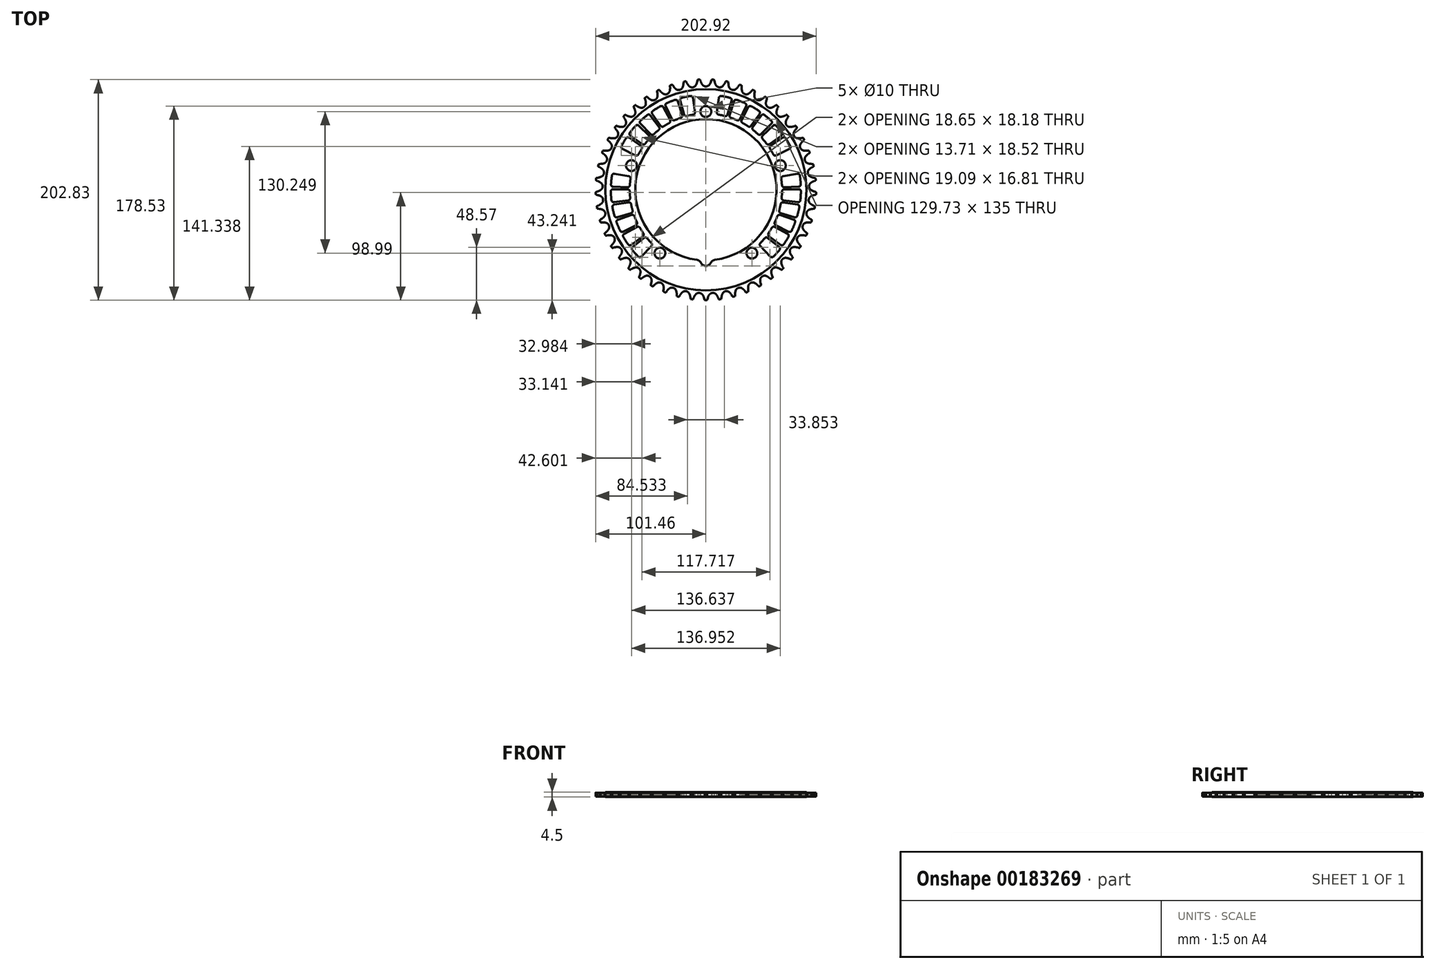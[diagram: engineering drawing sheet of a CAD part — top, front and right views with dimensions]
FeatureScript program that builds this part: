
annotation { "Feature Type Name" : "Feature", "Feature Type Description" : "" }
export const myFeature = defineFeature(function(context is Context, id is Id, definition is map)
    precondition{}
    {
        {
            var Q0;
            Q0=qCreatedBy(makeId("Top.planeOp"),FACE);
            var sketch = newSketch(context, id + "F0", { "sketchPlane" : qUnion([Q0])});
            skCircle(sketch, "E0", {"center": v(0, 0) * mm, "radius": 65 * mm});
            skCircle(sketch, "E1", {"center": v(0, 72) * mm, "radius": 5 * mm});
            skCircle(sketch, "E2.1.0", {"center": v(-68.48, 22.25) * mm, "radius": 5 * mm});
            skCircle(sketch, "E2.2.0", {"center": v(-42.32, -58.25) * mm, "radius": 5 * mm});
            skCircle(sketch, "E2.3.0", {"center": v(42.32, -58.25) * mm, "radius": 5 * mm});
            skCircle(sketch, "E2.4.0", {"center": v(68.48, 22.25) * mm, "radius": 5 * mm});
            skArc(sketch, "E3", {"start": v(-3.24, 96.67) * mm, "mid": v(-1.82, 95.46) * mm, "end": v(0, 95.03) * mm});
            skCircle(sketch, "E4", {"center": v(0, 0) * mm, "radius": 92.53 * mm});
            skCircle(sketch, "E5", {"center": v(0, -65) * mm, "radius": 5 * mm});
            skArc(sketch, "E6", {"start": v(-4.67, 99.35) * mm, "mid": v(-4.06, 97.96) * mm, "end": v(-3.24, 96.67) * mm});
            skLineSegment(sketch, "E7", {"start": v(-4.67, 99.35) * mm, "end": v(-5.06, 100.45) * mm});
            skArc(sketch, "E8", {"start": v(-5.06, 100.45) * mm, "mid": v(-5.7, 101.76) * mm, "end": v(-6.6, 102.9) * mm});
            skArc(sketch, "E9.MirrorCS", {"start": v(5.06, 100.45) * mm, "mid": v(5.7, 101.76) * mm, "end": v(6.6, 102.9) * mm});
            skLineSegment(sketch, "E10.MirrorCS", {"start": v(4.67, 99.35) * mm, "end": v(5.06, 100.45) * mm});
            skArc(sketch, "E11.MirrorCS", {"start": v(4.67, 99.35) * mm, "mid": v(4.06, 97.96) * mm, "end": v(3.24, 96.67) * mm});
            skArc(sketch, "E12.MirrorCS", {"start": v(3.24, 96.67) * mm, "mid": v(1.82, 95.46) * mm, "end": v(0, 95.03) * mm});
            skArc(sketch, "E13.1.0", {"start": v(-17.87, 98.98) * mm, "mid": v(-18.66, 100.2) * mm, "end": v(-19.7, 101.2) * mm});
            skLineSegment(sketch, "E13.1.1", {"start": v(-17.34, 97.94) * mm, "end": v(-17.87, 98.98) * mm});
            skArc(sketch, "E13.1.2", {"start": v(-17.34, 97.94) * mm, "mid": v(-16.55, 96.64) * mm, "end": v(-15.57, 95.46) * mm});
            skArc(sketch, "E13.1.3", {"start": v(-15.57, 95.46) * mm, "mid": v(-14, 94.45) * mm, "end": v(-12.15, 94.25) * mm});
            skArc(sketch, "E13.1.4", {"start": v(-9.15, 96.29) * mm, "mid": v(-10.4, 94.9) * mm, "end": v(-12.15, 94.25) * mm});
            skArc(sketch, "E13.1.5", {"start": v(-8.07, 99.14) * mm, "mid": v(-8.5, 97.67) * mm, "end": v(-9.15, 96.29) * mm});
            skLineSegment(sketch, "E13.1.6", {"start": v(-8.07, 99.14) * mm, "end": v(-7.83, 100.28) * mm});
            skArc(sketch, "E13.1.7", {"start": v(-7.83, 100.28) * mm, "mid": v(-7.37, 101.65) * mm, "end": v(-6.6, 102.9) * mm});
            skArc(sketch, "E13.2.0", {"start": v(-30.38, 95.89) * mm, "mid": v(-31.32, 96.99) * mm, "end": v(-32.49, 97.85) * mm});
            skLineSegment(sketch, "E13.2.1", {"start": v(-29.72, 94.92) * mm, "end": v(-30.38, 95.89) * mm});
            skArc(sketch, "E13.2.2", {"start": v(-29.72, 94.92) * mm, "mid": v(-28.77, 93.73) * mm, "end": v(-27.65, 92.69) * mm});
            skArc(sketch, "E13.2.3", {"start": v(-27.65, 92.69) * mm, "mid": v(-25.97, 91.88) * mm, "end": v(-24.1, 91.92) * mm});
            skArc(sketch, "E13.2.4", {"start": v(-21.39, 94.33) * mm, "mid": v(-22.46, 92.8) * mm, "end": v(-24.1, 91.92) * mm});
            skArc(sketch, "E13.2.5", {"start": v(-20.68, 97.3) * mm, "mid": v(-20.92, 95.78) * mm, "end": v(-21.39, 94.33) * mm});
            skLineSegment(sketch, "E13.2.6", {"start": v(-20.68, 97.3) * mm, "end": v(-20.59, 98.45) * mm});
            skArc(sketch, "E13.2.7", {"start": v(-20.59, 98.45) * mm, "mid": v(-20.3, 99.88) * mm, "end": v(-19.7, 101.2) * mm});
            skArc(sketch, "E13.3.0", {"start": v(-42.39, 91.21) * mm, "mid": v(-43.47, 92.19) * mm, "end": v(-44.73, 92.9) * mm});
            skLineSegment(sketch, "E13.3.1", {"start": v(-41.62, 90.34) * mm, "end": v(-42.39, 91.21) * mm});
            skArc(sketch, "E13.3.2", {"start": v(-41.62, 90.34) * mm, "mid": v(-40.52, 89.28) * mm, "end": v(-39.28, 88.39) * mm});
            skArc(sketch, "E13.3.3", {"start": v(-39.28, 88.39) * mm, "mid": v(-37.5, 87.8) * mm, "end": v(-35.66, 88.08) * mm});
            skArc(sketch, "E13.3.4", {"start": v(-33.27, 90.82) * mm, "mid": v(-34.14, 89.17) * mm, "end": v(-35.66, 88.08) * mm});
            skArc(sketch, "E13.3.5", {"start": v(-32.95, 93.85) * mm, "mid": v(-33, 92.32) * mm, "end": v(-33.27, 90.82) * mm});
            skLineSegment(sketch, "E13.3.6", {"start": v(-32.95, 93.85) * mm, "end": v(-33, 95.01) * mm});
            skArc(sketch, "E13.3.7", {"start": v(-33, 95.01) * mm, "mid": v(-32.9, 96.46) * mm, "end": v(-32.49, 97.85) * mm});
            skArc(sketch, "E13.4.0", {"start": v(-53.7, 85.04) * mm, "mid": v(-54.9, 85.87) * mm, "end": v(-56.25, 86.4) * mm});
            skLineSegment(sketch, "E13.4.1", {"start": v(-52.83, 84.28) * mm, "end": v(-53.7, 85.04) * mm});
            skArc(sketch, "E13.4.2", {"start": v(-52.83, 84.28) * mm, "mid": v(-51.6, 83.36) * mm, "end": v(-50.26, 82.64) * mm});
            skArc(sketch, "E13.4.3", {"start": v(-50.26, 82.64) * mm, "mid": v(-48.43, 82.29) * mm, "end": v(-46.63, 82.8) * mm});
            skArc(sketch, "E13.4.4", {"start": v(-44.62, 85.82) * mm, "mid": v(-45.26, 84.07) * mm, "end": v(-46.63, 82.8) * mm});
            skArc(sketch, "E13.4.5", {"start": v(-44.68, 88.86) * mm, "mid": v(-44.54, 87.34) * mm, "end": v(-44.62, 85.82) * mm});
            skLineSegment(sketch, "E13.4.6", {"start": v(-44.68, 88.86) * mm, "end": v(-44.88, 90.01) * mm});
            skArc(sketch, "E13.4.7", {"start": v(-44.88, 90.01) * mm, "mid": v(-44.97, 91.46) * mm, "end": v(-44.73, 92.9) * mm});
            skArc(sketch, "E13.5.0", {"start": v(-64.14, 77.48) * mm, "mid": v(-65.43, 78.15) * mm, "end": v(-66.83, 78.5) * mm});
            skLineSegment(sketch, "E13.5.1", {"start": v(-63.17, 76.83) * mm, "end": v(-64.14, 77.48) * mm});
            skArc(sketch, "E13.5.2", {"start": v(-63.17, 76.83) * mm, "mid": v(-61.84, 76.08) * mm, "end": v(-60.41, 75.53) * mm});
            skArc(sketch, "E13.5.3", {"start": v(-60.41, 75.53) * mm, "mid": v(-58.55, 75.42) * mm, "end": v(-56.84, 76.16) * mm});
            skArc(sketch, "E13.5.4", {"start": v(-55.22, 79.4) * mm, "mid": v(-55.64, 77.59) * mm, "end": v(-56.84, 76.16) * mm});
            skArc(sketch, "E13.5.5", {"start": v(-55.68, 82.42) * mm, "mid": v(-55.34, 80.93) * mm, "end": v(-55.22, 79.4) * mm});
            skLineSegment(sketch, "E13.5.6", {"start": v(-55.68, 82.42) * mm, "end": v(-56.03, 83.53) * mm});
            skArc(sketch, "E13.5.7", {"start": v(-56.03, 83.53) * mm, "mid": v(-56.3, 84.96) * mm, "end": v(-56.25, 86.4) * mm});
            skArc(sketch, "E13.6.0", {"start": v(-73.52, 68.64) * mm, "mid": v(-74.88, 69.14) * mm, "end": v(-76.32, 69.32) * mm});
            skLineSegment(sketch, "E13.6.1", {"start": v(-72.48, 68.12) * mm, "end": v(-73.52, 68.64) * mm});
            skArc(sketch, "E13.6.2", {"start": v(-72.48, 68.12) * mm, "mid": v(-71.06, 67.55) * mm, "end": v(-69.58, 67.19) * mm});
            skArc(sketch, "E13.6.3", {"start": v(-69.58, 67.19) * mm, "mid": v(-67.71, 67.31) * mm, "end": v(-66.1, 68.26) * mm});
            skArc(sketch, "E13.6.4", {"start": v(-64.92, 71.7) * mm, "mid": v(-65.1, 69.84) * mm, "end": v(-66.1, 68.26) * mm});
            skArc(sketch, "E13.6.5", {"start": v(-65.76, 74.62) * mm, "mid": v(-65.23, 73.2) * mm, "end": v(-64.92, 71.7) * mm});
            skLineSegment(sketch, "E13.6.6", {"start": v(-65.76, 74.62) * mm, "end": v(-66.25, 75.68) * mm});
            skArc(sketch, "E13.6.7", {"start": v(-66.25, 75.68) * mm, "mid": v(-66.7, 77.06) * mm, "end": v(-66.83, 78.5) * mm});
            skArc(sketch, "E13.7.0", {"start": v(-81.7, 58.68) * mm, "mid": v(-83.11, 59) * mm, "end": v(-84.56, 58.99) * mm});
            skLineSegment(sketch, "E13.7.1", {"start": v(-80.6, 58.3) * mm, "end": v(-81.7, 58.68) * mm});
            skArc(sketch, "E13.7.2", {"start": v(-80.6, 58.3) * mm, "mid": v(-79.12, 57.9) * mm, "end": v(-77.6, 57.74) * mm});
            skArc(sketch, "E13.7.3", {"start": v(-77.6, 57.74) * mm, "mid": v(-75.77, 58.1) * mm, "end": v(-74.3, 59.25) * mm});
            skArc(sketch, "E13.7.4", {"start": v(-73.56, 62.8) * mm, "mid": v(-73.5, 60.94) * mm, "end": v(-74.3, 59.25) * mm});
            skArc(sketch, "E13.7.5", {"start": v(-74.76, 65.6) * mm, "mid": v(-74.06, 64.25) * mm, "end": v(-73.56, 62.8) * mm});
            skLineSegment(sketch, "E13.7.6", {"start": v(-74.76, 65.6) * mm, "end": v(-75.38, 66.59) * mm});
            skArc(sketch, "E13.7.7", {"start": v(-75.38, 66.59) * mm, "mid": v(-76, 67.9) * mm, "end": v(-76.32, 69.32) * mm});
            skArc(sketch, "E13.8.0", {"start": v(-88.53, 47.75) * mm, "mid": v(-89.97, 47.88) * mm, "end": v(-91.41, 47.69) * mm});
            skLineSegment(sketch, "E13.8.1", {"start": v(-87.38, 47.5) * mm, "end": v(-88.53, 47.75) * mm});
            skArc(sketch, "E13.8.2", {"start": v(-87.38, 47.5) * mm, "mid": v(-85.87, 47.31) * mm, "end": v(-84.35, 47.34) * mm});
            skArc(sketch, "E13.8.3", {"start": v(-84.35, 47.34) * mm, "mid": v(-82.57, 47.93) * mm, "end": v(-81.26, 49.26) * mm});
            skArc(sketch, "E13.8.4", {"start": v(-80.99, 52.88) * mm, "mid": v(-80.7, 51.04) * mm, "end": v(-81.26, 49.26) * mm});
            skArc(sketch, "E13.8.5", {"start": v(-82.54, 55.5) * mm, "mid": v(-81.67, 54.25) * mm, "end": v(-80.99, 52.88) * mm});
            skLineSegment(sketch, "E13.8.6", {"start": v(-82.54, 55.5) * mm, "end": v(-83.28, 56.4) * mm});
            skArc(sketch, "E13.8.7", {"start": v(-83.28, 56.4) * mm, "mid": v(-84.07, 57.62) * mm, "end": v(-84.56, 58.99) * mm});
            skArc(sketch, "E13.9.0", {"start": v(-93.9, 36.03) * mm, "mid": v(-95.36, 35.98) * mm, "end": v(-96.76, 35.6) * mm});
            skLineSegment(sketch, "E13.9.1", {"start": v(-92.74, 35.94) * mm, "end": v(-93.9, 36.03) * mm});
            skArc(sketch, "E13.9.2", {"start": v(-92.74, 35.94) * mm, "mid": v(-91.22, 35.94) * mm, "end": v(-89.7, 36.17) * mm});
            skArc(sketch, "E13.9.3", {"start": v(-89.7, 36.17) * mm, "mid": v(-88.03, 36.98) * mm, "end": v(-86.9, 38.47) * mm});
            skArc(sketch, "E13.9.4", {"start": v(-87.08, 42.1) * mm, "mid": v(-86.56, 40.3) * mm, "end": v(-86.9, 38.47) * mm});
            skArc(sketch, "E13.9.5", {"start": v(-88.96, 44.5) * mm, "mid": v(-87.93, 43.36) * mm, "end": v(-87.08, 42.1) * mm});
            skLineSegment(sketch, "E13.9.6", {"start": v(-88.96, 44.5) * mm, "end": v(-89.8, 45.3) * mm});
            skArc(sketch, "E13.9.7", {"start": v(-89.8, 45.3) * mm, "mid": v(-90.75, 46.4) * mm, "end": v(-91.41, 47.69) * mm});
            skArc(sketch, "E13.10.0", {"start": v(-97.74, 23.73) * mm, "mid": v(-99.17, 23.5) * mm, "end": v(-100.52, 22.94) * mm});
            skLineSegment(sketch, "E13.10.1", {"start": v(-96.58, 23.79) * mm, "end": v(-97.74, 23.73) * mm});
            skArc(sketch, "E13.10.2", {"start": v(-96.58, 23.79) * mm, "mid": v(-95.06, 23.98) * mm, "end": v(-93.6, 24.4) * mm});
            skArc(sketch, "E13.10.3", {"start": v(-93.6, 24.4) * mm, "mid": v(-92.03, 25.42) * mm, "end": v(-91.1, 27.04) * mm});
            skArc(sketch, "E13.10.4", {"start": v(-91.75, 30.61) * mm, "mid": v(-91, 28.9) * mm, "end": v(-91.1, 27.04) * mm});
            skArc(sketch, "E13.10.5", {"start": v(-93.92, 32.75) * mm, "mid": v(-92.76, 31.76) * mm, "end": v(-91.75, 30.61) * mm});
            skLineSegment(sketch, "E13.10.6", {"start": v(-93.92, 32.75) * mm, "end": v(-94.86, 33.43) * mm});
            skArc(sketch, "E13.10.7", {"start": v(-94.86, 33.43) * mm, "mid": v(-95.93, 34.41) * mm, "end": v(-96.76, 35.6) * mm});
            skArc(sketch, "E13.11.0", {"start": v(-99.97, 11.04) * mm, "mid": v(-101.37, 10.62) * mm, "end": v(-102.63, 9.9) * mm});
            skLineSegment(sketch, "E13.11.1", {"start": v(-98.83, 11.24) * mm, "end": v(-99.97, 11.04) * mm});
            skArc(sketch, "E13.11.2", {"start": v(-98.83, 11.24) * mm, "mid": v(-97.35, 11.63) * mm, "end": v(-95.95, 12.23) * mm});
            skArc(sketch, "E13.11.3", {"start": v(-95.95, 12.23) * mm, "mid": v(-94.53, 13.44) * mm, "end": v(-93.8, 15.17) * mm});
            skArc(sketch, "E13.11.4", {"start": v(-94.91, 18.63) * mm, "mid": v(-93.95, 17.03) * mm, "end": v(-93.8, 15.17) * mm});
            skArc(sketch, "E13.11.5", {"start": v(-97.33, 20.47) * mm, "mid": v(-96.06, 19.64) * mm, "end": v(-94.91, 18.63) * mm});
            skLineSegment(sketch, "E13.11.6", {"start": v(-97.33, 20.47) * mm, "end": v(-98.36, 21.03) * mm});
            skArc(sketch, "E13.11.7", {"start": v(-98.36, 21.03) * mm, "mid": v(-99.55, 21.86) * mm, "end": v(-100.52, 22.94) * mm});
            skArc(sketch, "E13.12.0", {"start": v(-100.56, -1.84) * mm, "mid": v(-101.9, -2.43) * mm, "end": v(-103.05, -3.3) * mm});
            skLineSegment(sketch, "E13.12.1", {"start": v(-99.45, -1.49) * mm, "end": v(-100.56, -1.84) * mm});
            skArc(sketch, "E13.12.2", {"start": v(-99.45, -1.49) * mm, "mid": v(-98.04, -0.91) * mm, "end": v(-96.72, -0.14) * mm});
            skArc(sketch, "E13.12.3", {"start": v(-96.72, -0.14) * mm, "mid": v(-95.47, 1.24) * mm, "end": v(-94.98, 3.05) * mm});
            skArc(sketch, "E13.12.4", {"start": v(-96.52, 6.34) * mm, "mid": v(-95.35, 4.87) * mm, "end": v(-94.98, 3.05) * mm});
            skArc(sketch, "E13.12.5", {"start": v(-99.15, 7.86) * mm, "mid": v(-97.78, 7.2) * mm, "end": v(-96.52, 6.34) * mm});
            skLineSegment(sketch, "E13.12.6", {"start": v(-99.15, 7.86) * mm, "end": v(-100.24, 8.28) * mm});
            skArc(sketch, "E13.12.7", {"start": v(-100.24, 8.28) * mm, "mid": v(-101.53, 8.95) * mm, "end": v(-102.63, 9.9) * mm});
            skArc(sketch, "E13.13.0", {"start": v(-99.5, -14.68) * mm, "mid": v(-100.74, -15.44) * mm, "end": v(-101.78, -16.46) * mm});
            skLineSegment(sketch, "E13.13.1", {"start": v(-98.45, -14.2) * mm, "end": v(-99.5, -14.68) * mm});
            skArc(sketch, "E13.13.2", {"start": v(-98.45, -14.2) * mm, "mid": v(-97.12, -13.44) * mm, "end": v(-95.91, -12.5) * mm});
            skArc(sketch, "E13.13.3", {"start": v(-95.91, -12.5) * mm, "mid": v(-94.85, -10.97) * mm, "end": v(-94.59, -9.12) * mm});
            skArc(sketch, "E13.13.4", {"start": v(-96.53, -6.06) * mm, "mid": v(-95.2, -7.36) * mm, "end": v(-94.59, -9.12) * mm});
            skArc(sketch, "E13.13.5", {"start": v(-99.34, -4.89) * mm, "mid": v(-97.9, -5.37) * mm, "end": v(-96.53, -6.06) * mm});
            skLineSegment(sketch, "E13.13.6", {"start": v(-99.34, -4.89) * mm, "end": v(-100.48, -4.6) * mm});
            skArc(sketch, "E13.13.7", {"start": v(-100.48, -4.6) * mm, "mid": v(-101.84, -4.1) * mm, "end": v(-103.05, -3.3) * mm});
            skArc(sketch, "E13.14.0", {"start": v(-96.8, -27.29) * mm, "mid": v(-97.94, -28.2) * mm, "end": v(-98.84, -29.34) * mm});
            skLineSegment(sketch, "E13.14.1", {"start": v(-95.82, -26.67) * mm, "end": v(-96.8, -27.29) * mm});
            skArc(sketch, "E13.14.2", {"start": v(-95.82, -26.67) * mm, "mid": v(-94.6, -25.75) * mm, "end": v(-93.52, -24.67) * mm});
            skArc(sketch, "E13.14.3", {"start": v(-93.52, -24.67) * mm, "mid": v(-92.66, -23.01) * mm, "end": v(-92.64, -21.15) * mm});
            skArc(sketch, "E13.14.4", {"start": v(-94.97, -18.35) * mm, "mid": v(-93.47, -19.47) * mm, "end": v(-92.64, -21.15) * mm});
            skArc(sketch, "E13.14.5", {"start": v(-97.9, -17.55) * mm, "mid": v(-96.4, -17.84) * mm, "end": v(-94.97, -18.35) * mm});
            skLineSegment(sketch, "E13.14.6", {"start": v(-97.9, -17.55) * mm, "end": v(-99.06, -17.42) * mm});
            skArc(sketch, "E13.14.7", {"start": v(-99.06, -17.42) * mm, "mid": v(-100.48, -17.1) * mm, "end": v(-101.78, -16.46) * mm});
            skArc(sketch, "E13.15.0", {"start": v(-92.53, -39.44) * mm, "mid": v(-93.53, -40.49) * mm, "end": v(-94.28, -41.73) * mm});
            skLineSegment(sketch, "E13.15.1", {"start": v(-91.63, -38.7) * mm, "end": v(-92.53, -39.44) * mm});
            skArc(sketch, "E13.15.2", {"start": v(-91.63, -38.7) * mm, "mid": v(-90.53, -37.64) * mm, "end": v(-89.6, -36.43) * mm});
            skArc(sketch, "E13.15.3", {"start": v(-89.6, -36.43) * mm, "mid": v(-88.96, -34.67) * mm, "end": v(-89.18, -32.82) * mm});
            skArc(sketch, "E13.15.4", {"start": v(-91.84, -30.35) * mm, "mid": v(-90.21, -31.26) * mm, "end": v(-89.18, -32.82) * mm});
            skArc(sketch, "E13.15.5", {"start": v(-94.85, -29.93) * mm, "mid": v(-93.33, -30.03) * mm, "end": v(-91.84, -30.35) * mm});
            skLineSegment(sketch, "E13.15.6", {"start": v(-94.85, -29.93) * mm, "end": v(-96.02, -29.94) * mm});
            skArc(sketch, "E13.15.7", {"start": v(-96.02, -29.94) * mm, "mid": v(-97.47, -29.8) * mm, "end": v(-98.84, -29.34) * mm});
            skArc(sketch, "E13.16.0", {"start": v(-86.72, -50.95) * mm, "mid": v(-87.59, -52.12) * mm, "end": v(-88.17, -53.45) * mm});
            skLineSegment(sketch, "E13.16.1", {"start": v(-85.93, -50.1) * mm, "end": v(-86.72, -50.95) * mm});
            skArc(sketch, "E13.16.2", {"start": v(-85.93, -50.1) * mm, "mid": v(-84.97, -48.9) * mm, "end": v(-84.2, -47.59) * mm});
            skArc(sketch, "E13.16.3", {"start": v(-84.2, -47.59) * mm, "mid": v(-83.8, -45.76) * mm, "end": v(-84.25, -43.95) * mm});
            skArc(sketch, "E13.16.4", {"start": v(-87.2, -41.84) * mm, "mid": v(-85.48, -42.54) * mm, "end": v(-84.25, -43.95) * mm});
            skArc(sketch, "E13.16.5", {"start": v(-90.25, -41.81) * mm, "mid": v(-88.73, -41.71) * mm, "end": v(-87.2, -41.84) * mm});
            skLineSegment(sketch, "E13.16.6", {"start": v(-90.25, -41.81) * mm, "end": v(-91.4, -41.98) * mm});
            skArc(sketch, "E13.16.7", {"start": v(-91.4, -41.98) * mm, "mid": v(-92.85, -42.02) * mm, "end": v(-94.28, -41.73) * mm});
            skArc(sketch, "E13.17.0", {"start": v(-79.5, -61.62) * mm, "mid": v(-80.2, -62.89) * mm, "end": v(-80.6, -64.28) * mm});
            skLineSegment(sketch, "E13.17.1", {"start": v(-78.81, -60.68) * mm, "end": v(-79.5, -61.62) * mm});
            skArc(sketch, "E13.17.2", {"start": v(-78.81, -60.68) * mm, "mid": v(-78.02, -59.37) * mm, "end": v(-77.43, -57.96) * mm});
            skArc(sketch, "E13.17.3", {"start": v(-77.43, -57.96) * mm, "mid": v(-77.26, -56.1) * mm, "end": v(-77.94, -54.37) * mm});
            skArc(sketch, "E13.17.4", {"start": v(-81.14, -52.65) * mm, "mid": v(-79.33, -53.13) * mm, "end": v(-77.94, -54.37) * mm});
            skArc(sketch, "E13.17.5", {"start": v(-84.16, -53) * mm, "mid": v(-82.66, -52.72) * mm, "end": v(-81.14, -52.65) * mm});
            skLineSegment(sketch, "E13.17.6", {"start": v(-84.16, -53) * mm, "end": v(-85.29, -53.32) * mm});
            skArc(sketch, "E13.17.7", {"start": v(-85.29, -53.32) * mm, "mid": v(-86.72, -53.55) * mm, "end": v(-88.17, -53.45) * mm});
            skArc(sketch, "E13.18.0", {"start": v(-70.96, -71.28) * mm, "mid": v(-71.5, -72.63) * mm, "end": v(-71.73, -74.06) * mm});
            skLineSegment(sketch, "E13.18.1", {"start": v(-70.4, -70.26) * mm, "end": v(-70.96, -71.28) * mm});
            skArc(sketch, "E13.18.2", {"start": v(-70.4, -70.26) * mm, "mid": v(-69.8, -68.86) * mm, "end": v(-69.38, -67.39) * mm});
            skArc(sketch, "E13.18.3", {"start": v(-69.38, -67.39) * mm, "mid": v(-69.45, -65.52) * mm, "end": v(-70.35, -63.89) * mm});
            skArc(sketch, "E13.18.4", {"start": v(-73.74, -62.6) * mm, "mid": v(-71.89, -62.83) * mm, "end": v(-70.35, -63.89) * mm});
            skArc(sketch, "E13.18.5", {"start": v(-76.7, -63.34) * mm, "mid": v(-75.24, -62.86) * mm, "end": v(-73.74, -62.6) * mm});
            skLineSegment(sketch, "E13.18.6", {"start": v(-76.7, -63.34) * mm, "end": v(-77.77, -63.79) * mm});
            skArc(sketch, "E13.18.7", {"start": v(-77.77, -63.79) * mm, "mid": v(-79.16, -64.2) * mm, "end": v(-80.6, -64.28) * mm});
            skArc(sketch, "E13.19.0", {"start": v(-61.26, -79.77) * mm, "mid": v(-61.63, -81.18) * mm, "end": v(-61.67, -82.63) * mm});
            skLineSegment(sketch, "E13.19.1", {"start": v(-60.84, -78.68) * mm, "end": v(-61.26, -79.77) * mm});
            skArc(sketch, "E13.19.2", {"start": v(-60.84, -78.68) * mm, "mid": v(-60.41, -77.22) * mm, "end": v(-60.2, -75.7) * mm});
            skArc(sketch, "E13.19.3", {"start": v(-60.2, -75.7) * mm, "mid": v(-60.5, -73.87) * mm, "end": v(-61.6, -72.36) * mm});
            skArc(sketch, "E13.19.4", {"start": v(-65.13, -71.5) * mm, "mid": v(-63.26, -71.51) * mm, "end": v(-61.6, -72.36) * mm});
            skArc(sketch, "E13.19.5", {"start": v(-67.96, -72.62) * mm, "mid": v(-66.59, -71.96) * mm, "end": v(-65.13, -71.5) * mm});
            skLineSegment(sketch, "E13.19.6", {"start": v(-67.96, -72.62) * mm, "end": v(-68.97, -73.2) * mm});
            skArc(sketch, "E13.19.7", {"start": v(-68.97, -73.2) * mm, "mid": v(-70.3, -73.8) * mm, "end": v(-71.73, -74.06) * mm});
            skArc(sketch, "E13.20.0", {"start": v(-50.56, -86.95) * mm, "mid": v(-50.74, -88.4) * mm, "end": v(-50.6, -89.84) * mm});
            skLineSegment(sketch, "E13.20.1", {"start": v(-50.28, -85.82) * mm, "end": v(-50.56, -86.95) * mm});
            skArc(sketch, "E13.20.2", {"start": v(-50.28, -85.82) * mm, "mid": v(-50.04, -84.31) * mm, "end": v(-50.02, -82.78) * mm});
            skArc(sketch, "E13.20.3", {"start": v(-50.02, -82.78) * mm, "mid": v(-50.56, -81) * mm, "end": v(-51.84, -79.64) * mm});
            skArc(sketch, "E13.20.4", {"start": v(-55.45, -79.25) * mm, "mid": v(-53.6, -79.01) * mm, "end": v(-51.84, -79.64) * mm});
            skArc(sketch, "E13.20.5", {"start": v(-58.12, -80.72) * mm, "mid": v(-56.84, -79.89) * mm, "end": v(-55.45, -79.25) * mm});
            skLineSegment(sketch, "E13.20.6", {"start": v(-58.12, -80.72) * mm, "end": v(-59.04, -81.43) * mm});
            skArc(sketch, "E13.20.7", {"start": v(-59.04, -81.43) * mm, "mid": v(-60.29, -82.18) * mm, "end": v(-61.67, -82.63) * mm});
            skArc(sketch, "E13.21.0", {"start": v(-39.03, -92.7) * mm, "mid": v(-39.02, -94.15) * mm, "end": v(-38.7, -95.57) * mm});
            skLineSegment(sketch, "E13.21.1", {"start": v(-38.9, -91.54) * mm, "end": v(-39.03, -92.7) * mm});
            skArc(sketch, "E13.21.2", {"start": v(-38.9, -91.54) * mm, "mid": v(-38.85, -90.02) * mm, "end": v(-39.02, -88.5) * mm});
            skArc(sketch, "E13.21.3", {"start": v(-39.02, -88.5) * mm, "mid": v(-39.78, -86.8) * mm, "end": v(-41.23, -85.62) * mm});
            skArc(sketch, "E13.21.4", {"start": v(-44.86, -85.7) * mm, "mid": v(-43.05, -85.22) * mm, "end": v(-41.23, -85.62) * mm});
            skArc(sketch, "E13.21.5", {"start": v(-47.32, -87.49) * mm, "mid": v(-46.16, -86.5) * mm, "end": v(-44.86, -85.7) * mm});
            skLineSegment(sketch, "E13.21.6", {"start": v(-47.32, -87.49) * mm, "end": v(-48.15, -88.31) * mm});
            skArc(sketch, "E13.21.7", {"start": v(-48.15, -88.31) * mm, "mid": v(-49.28, -89.21) * mm, "end": v(-50.6, -89.84) * mm});
            skArc(sketch, "E13.22.0", {"start": v(-26.85, -96.93) * mm, "mid": v(-26.66, -98.37) * mm, "end": v(-26.15, -99.73) * mm});
            skLineSegment(sketch, "E13.22.1", {"start": v(-26.87, -95.77) * mm, "end": v(-26.85, -96.93) * mm});
            skArc(sketch, "E13.22.2", {"start": v(-26.87, -95.77) * mm, "mid": v(-27.02, -94.25) * mm, "end": v(-27.39, -92.77) * mm});
            skArc(sketch, "E13.22.3", {"start": v(-27.39, -92.77) * mm, "mid": v(-28.36, -91.17) * mm, "end": v(-29.94, -90.19) * mm});
            skArc(sketch, "E13.22.4", {"start": v(-33.54, -90.72) * mm, "mid": v(-31.8, -90.03) * mm, "end": v(-29.94, -90.19) * mm});
            skArc(sketch, "E13.22.5", {"start": v(-35.74, -92.82) * mm, "mid": v(-34.72, -91.7) * mm, "end": v(-33.54, -90.72) * mm});
            skLineSegment(sketch, "E13.22.6", {"start": v(-35.74, -92.82) * mm, "end": v(-36.46, -93.74) * mm});
            skArc(sketch, "E13.22.7", {"start": v(-36.46, -93.74) * mm, "mid": v(-37.47, -94.78) * mm, "end": v(-38.7, -95.57) * mm});
            skArc(sketch, "E13.23.0", {"start": v(-14.23, -99.57) * mm, "mid": v(-13.86, -100.97) * mm, "end": v(-13.18, -102.26) * mm});
            skLineSegment(sketch, "E13.23.1", {"start": v(-14.4, -98.42) * mm, "end": v(-14.23, -99.57) * mm});
            skArc(sketch, "E13.23.2", {"start": v(-14.4, -98.42) * mm, "mid": v(-14.74, -96.93) * mm, "end": v(-15.3, -95.5) * mm});
            skArc(sketch, "E13.23.3", {"start": v(-15.3, -95.5) * mm, "mid": v(-16.47, -94.05) * mm, "end": v(-18.17, -93.27) * mm});
            skArc(sketch, "E13.23.4", {"start": v(-21.66, -94.27) * mm, "mid": v(-20.03, -93.35) * mm, "end": v(-18.17, -93.27) * mm});
            skArc(sketch, "E13.23.5", {"start": v(-23.58, -96.63) * mm, "mid": v(-22.7, -95.38) * mm, "end": v(-21.66, -94.27) * mm});
            skLineSegment(sketch, "E13.23.6", {"start": v(-23.58, -96.63) * mm, "end": v(-24.17, -97.63) * mm});
            skArc(sketch, "E13.23.7", {"start": v(-24.17, -97.63) * mm, "mid": v(-25.04, -98.8) * mm, "end": v(-26.15, -99.73) * mm});
            skArc(sketch, "E13.24.0", {"start": v(-1.39, -100.57) * mm, "mid": v(-0.84, -101.92) * mm, "end": v(0, -103.1) * mm});
            skLineSegment(sketch, "E13.24.1", {"start": v(-1.7, -99.45) * mm, "end": v(-1.39, -100.57) * mm});
            skArc(sketch, "E13.24.2", {"start": v(-1.7, -99.45) * mm, "mid": v(-2.23, -98.02) * mm, "end": v(-2.96, -96.68) * mm});
            skArc(sketch, "E13.24.3", {"start": v(-2.96, -96.68) * mm, "mid": v(-4.3, -95.38) * mm, "end": v(-6.09, -94.83) * mm});
            skArc(sketch, "E13.24.4", {"start": v(-9.43, -96.26) * mm, "mid": v(-7.93, -95.15) * mm, "end": v(-6.09, -94.83) * mm});
            skArc(sketch, "E13.24.5", {"start": v(-11.03, -98.85) * mm, "mid": v(-10.32, -97.5) * mm, "end": v(-9.43, -96.26) * mm});
            skLineSegment(sketch, "E13.24.6", {"start": v(-11.03, -98.85) * mm, "end": v(-11.49, -99.92) * mm});
            skArc(sketch, "E13.24.7", {"start": v(-11.49, -99.92) * mm, "mid": v(-12.2, -101.19) * mm, "end": v(-13.18, -102.26) * mm});
            skArc(sketch, "E13.25.0", {"start": v(11.49, -99.92) * mm, "mid": v(12.2, -101.19) * mm, "end": v(13.18, -102.26) * mm});
            skLineSegment(sketch, "E13.25.1", {"start": v(11.03, -98.85) * mm, "end": v(11.49, -99.92) * mm});
            skArc(sketch, "E13.25.2", {"start": v(11.03, -98.85) * mm, "mid": v(10.32, -97.5) * mm, "end": v(9.43, -96.26) * mm});
            skArc(sketch, "E13.25.3", {"start": v(9.43, -96.26) * mm, "mid": v(7.93, -95.15) * mm, "end": v(6.09, -94.83) * mm});
            skArc(sketch, "E13.25.4", {"start": v(2.96, -96.68) * mm, "mid": v(4.3, -95.38) * mm, "end": v(6.09, -94.83) * mm});
            skArc(sketch, "E13.25.5", {"start": v(1.7, -99.45) * mm, "mid": v(2.23, -98.02) * mm, "end": v(2.96, -96.68) * mm});
            skLineSegment(sketch, "E13.25.6", {"start": v(1.7, -99.45) * mm, "end": v(1.39, -100.57) * mm});
            skArc(sketch, "E13.25.7", {"start": v(1.39, -100.57) * mm, "mid": v(0.84, -101.92) * mm, "end": v(0, -103.1) * mm});
            skArc(sketch, "E13.26.0", {"start": v(24.17, -97.63) * mm, "mid": v(25.04, -98.8) * mm, "end": v(26.15, -99.73) * mm});
            skLineSegment(sketch, "E13.26.1", {"start": v(23.58, -96.63) * mm, "end": v(24.17, -97.63) * mm});
            skArc(sketch, "E13.26.2", {"start": v(23.58, -96.63) * mm, "mid": v(22.7, -95.38) * mm, "end": v(21.66, -94.27) * mm});
            skArc(sketch, "E13.26.3", {"start": v(21.66, -94.27) * mm, "mid": v(20.03, -93.35) * mm, "end": v(18.17, -93.27) * mm});
            skArc(sketch, "E13.26.4", {"start": v(15.3, -95.5) * mm, "mid": v(16.47, -94.05) * mm, "end": v(18.17, -93.27) * mm});
            skArc(sketch, "E13.26.5", {"start": v(14.4, -98.42) * mm, "mid": v(14.74, -96.93) * mm, "end": v(15.3, -95.5) * mm});
            skLineSegment(sketch, "E13.26.6", {"start": v(14.4, -98.42) * mm, "end": v(14.23, -99.57) * mm});
            skArc(sketch, "E13.26.7", {"start": v(14.23, -99.57) * mm, "mid": v(13.86, -100.97) * mm, "end": v(13.18, -102.26) * mm});
            skArc(sketch, "E13.27.0", {"start": v(36.46, -93.74) * mm, "mid": v(37.47, -94.78) * mm, "end": v(38.7, -95.57) * mm});
            skLineSegment(sketch, "E13.27.1", {"start": v(35.74, -92.82) * mm, "end": v(36.46, -93.74) * mm});
            skArc(sketch, "E13.27.2", {"start": v(35.74, -92.82) * mm, "mid": v(34.72, -91.7) * mm, "end": v(33.54, -90.72) * mm});
            skArc(sketch, "E13.27.3", {"start": v(33.54, -90.72) * mm, "mid": v(31.8, -90.03) * mm, "end": v(29.94, -90.19) * mm});
            skArc(sketch, "E13.27.4", {"start": v(27.39, -92.77) * mm, "mid": v(28.36, -91.17) * mm, "end": v(29.94, -90.19) * mm});
            skArc(sketch, "E13.27.5", {"start": v(26.87, -95.77) * mm, "mid": v(27.02, -94.25) * mm, "end": v(27.39, -92.77) * mm});
            skLineSegment(sketch, "E13.27.6", {"start": v(26.87, -95.77) * mm, "end": v(26.85, -96.93) * mm});
            skArc(sketch, "E13.27.7", {"start": v(26.85, -96.93) * mm, "mid": v(26.66, -98.37) * mm, "end": v(26.15, -99.73) * mm});
            skArc(sketch, "E13.28.0", {"start": v(48.15, -88.31) * mm, "mid": v(49.28, -89.21) * mm, "end": v(50.6, -89.84) * mm});
            skLineSegment(sketch, "E13.28.1", {"start": v(47.32, -87.49) * mm, "end": v(48.15, -88.31) * mm});
            skArc(sketch, "E13.28.2", {"start": v(47.32, -87.49) * mm, "mid": v(46.16, -86.5) * mm, "end": v(44.86, -85.7) * mm});
            skArc(sketch, "E13.28.3", {"start": v(44.86, -85.7) * mm, "mid": v(43.05, -85.22) * mm, "end": v(41.23, -85.62) * mm});
            skArc(sketch, "E13.28.4", {"start": v(39.02, -88.5) * mm, "mid": v(39.78, -86.8) * mm, "end": v(41.23, -85.62) * mm});
            skArc(sketch, "E13.28.5", {"start": v(38.9, -91.54) * mm, "mid": v(38.85, -90.02) * mm, "end": v(39.02, -88.5) * mm});
            skLineSegment(sketch, "E13.28.6", {"start": v(38.9, -91.54) * mm, "end": v(39.03, -92.7) * mm});
            skArc(sketch, "E13.28.7", {"start": v(39.03, -92.7) * mm, "mid": v(39.02, -94.15) * mm, "end": v(38.7, -95.57) * mm});
            skArc(sketch, "E13.29.0", {"start": v(59.04, -81.43) * mm, "mid": v(60.29, -82.18) * mm, "end": v(61.67, -82.63) * mm});
            skLineSegment(sketch, "E13.29.1", {"start": v(58.12, -80.72) * mm, "end": v(59.04, -81.43) * mm});
            skArc(sketch, "E13.29.2", {"start": v(58.12, -80.72) * mm, "mid": v(56.84, -79.89) * mm, "end": v(55.45, -79.25) * mm});
            skArc(sketch, "E13.29.3", {"start": v(55.45, -79.25) * mm, "mid": v(53.6, -79.01) * mm, "end": v(51.84, -79.64) * mm});
            skArc(sketch, "E13.29.4", {"start": v(50.02, -82.78) * mm, "mid": v(50.56, -81) * mm, "end": v(51.84, -79.64) * mm});
            skArc(sketch, "E13.29.5", {"start": v(50.28, -85.82) * mm, "mid": v(50.04, -84.31) * mm, "end": v(50.02, -82.78) * mm});
            skLineSegment(sketch, "E13.29.6", {"start": v(50.28, -85.82) * mm, "end": v(50.56, -86.95) * mm});
            skArc(sketch, "E13.29.7", {"start": v(50.56, -86.95) * mm, "mid": v(50.74, -88.4) * mm, "end": v(50.6, -89.84) * mm});
            skArc(sketch, "E13.30.0", {"start": v(68.97, -73.2) * mm, "mid": v(70.3, -73.8) * mm, "end": v(71.73, -74.06) * mm});
            skLineSegment(sketch, "E13.30.1", {"start": v(67.96, -72.62) * mm, "end": v(68.97, -73.2) * mm});
            skArc(sketch, "E13.30.2", {"start": v(67.96, -72.62) * mm, "mid": v(66.59, -71.96) * mm, "end": v(65.13, -71.5) * mm});
            skArc(sketch, "E13.30.3", {"start": v(65.13, -71.5) * mm, "mid": v(63.26, -71.51) * mm, "end": v(61.6, -72.36) * mm});
            skArc(sketch, "E13.30.4", {"start": v(60.2, -75.7) * mm, "mid": v(60.5, -73.87) * mm, "end": v(61.6, -72.36) * mm});
            skArc(sketch, "E13.30.5", {"start": v(60.84, -78.68) * mm, "mid": v(60.41, -77.22) * mm, "end": v(60.2, -75.7) * mm});
            skLineSegment(sketch, "E13.30.6", {"start": v(60.84, -78.68) * mm, "end": v(61.26, -79.77) * mm});
            skArc(sketch, "E13.30.7", {"start": v(61.26, -79.77) * mm, "mid": v(61.63, -81.18) * mm, "end": v(61.67, -82.63) * mm});
            skArc(sketch, "E13.31.0", {"start": v(77.77, -63.79) * mm, "mid": v(79.16, -64.2) * mm, "end": v(80.6, -64.28) * mm});
            skLineSegment(sketch, "E13.31.1", {"start": v(76.7, -63.34) * mm, "end": v(77.77, -63.79) * mm});
            skArc(sketch, "E13.31.2", {"start": v(76.7, -63.34) * mm, "mid": v(75.24, -62.86) * mm, "end": v(73.74, -62.6) * mm});
            skArc(sketch, "E13.31.3", {"start": v(73.74, -62.6) * mm, "mid": v(71.89, -62.83) * mm, "end": v(70.35, -63.89) * mm});
            skArc(sketch, "E13.31.4", {"start": v(69.38, -67.39) * mm, "mid": v(69.45, -65.52) * mm, "end": v(70.35, -63.89) * mm});
            skArc(sketch, "E13.31.5", {"start": v(70.4, -70.26) * mm, "mid": v(69.8, -68.86) * mm, "end": v(69.38, -67.39) * mm});
            skLineSegment(sketch, "E13.31.6", {"start": v(70.4, -70.26) * mm, "end": v(70.96, -71.28) * mm});
            skArc(sketch, "E13.31.7", {"start": v(70.96, -71.28) * mm, "mid": v(71.5, -72.63) * mm, "end": v(71.73, -74.06) * mm});
            skArc(sketch, "E13.32.0", {"start": v(85.29, -53.32) * mm, "mid": v(86.72, -53.55) * mm, "end": v(88.17, -53.45) * mm});
            skLineSegment(sketch, "E13.32.1", {"start": v(84.16, -53) * mm, "end": v(85.29, -53.32) * mm});
            skArc(sketch, "E13.32.2", {"start": v(84.16, -53) * mm, "mid": v(82.66, -52.72) * mm, "end": v(81.14, -52.65) * mm});
            skArc(sketch, "E13.32.3", {"start": v(81.14, -52.65) * mm, "mid": v(79.33, -53.13) * mm, "end": v(77.94, -54.37) * mm});
            skArc(sketch, "E13.32.4", {"start": v(77.43, -57.96) * mm, "mid": v(77.26, -56.1) * mm, "end": v(77.94, -54.37) * mm});
            skArc(sketch, "E13.32.5", {"start": v(78.81, -60.68) * mm, "mid": v(78.02, -59.37) * mm, "end": v(77.43, -57.96) * mm});
            skLineSegment(sketch, "E13.32.6", {"start": v(78.81, -60.68) * mm, "end": v(79.5, -61.62) * mm});
            skArc(sketch, "E13.32.7", {"start": v(79.5, -61.62) * mm, "mid": v(80.2, -62.89) * mm, "end": v(80.6, -64.28) * mm});
            skArc(sketch, "E13.33.0", {"start": v(91.4, -41.98) * mm, "mid": v(92.85, -42.02) * mm, "end": v(94.28, -41.73) * mm});
            skLineSegment(sketch, "E13.33.1", {"start": v(90.25, -41.81) * mm, "end": v(91.4, -41.98) * mm});
            skArc(sketch, "E13.33.2", {"start": v(90.25, -41.81) * mm, "mid": v(88.73, -41.71) * mm, "end": v(87.2, -41.84) * mm});
            skArc(sketch, "E13.33.3", {"start": v(87.2, -41.84) * mm, "mid": v(85.48, -42.54) * mm, "end": v(84.25, -43.95) * mm});
            skArc(sketch, "E13.33.4", {"start": v(84.2, -47.59) * mm, "mid": v(83.8, -45.76) * mm, "end": v(84.25, -43.95) * mm});
            skArc(sketch, "E13.33.5", {"start": v(85.93, -50.1) * mm, "mid": v(84.97, -48.9) * mm, "end": v(84.2, -47.59) * mm});
            skLineSegment(sketch, "E13.33.6", {"start": v(85.93, -50.1) * mm, "end": v(86.72, -50.95) * mm});
            skArc(sketch, "E13.33.7", {"start": v(86.72, -50.95) * mm, "mid": v(87.59, -52.12) * mm, "end": v(88.17, -53.45) * mm});
            skArc(sketch, "E13.34.0", {"start": v(96.02, -29.94) * mm, "mid": v(97.47, -29.8) * mm, "end": v(98.84, -29.34) * mm});
            skLineSegment(sketch, "E13.34.1", {"start": v(94.85, -29.93) * mm, "end": v(96.02, -29.94) * mm});
            skArc(sketch, "E13.34.2", {"start": v(94.85, -29.93) * mm, "mid": v(93.33, -30.03) * mm, "end": v(91.84, -30.35) * mm});
            skArc(sketch, "E13.34.3", {"start": v(91.84, -30.35) * mm, "mid": v(90.21, -31.26) * mm, "end": v(89.18, -32.82) * mm});
            skArc(sketch, "E13.34.4", {"start": v(89.6, -36.43) * mm, "mid": v(88.96, -34.67) * mm, "end": v(89.18, -32.82) * mm});
            skArc(sketch, "E13.34.5", {"start": v(91.63, -38.7) * mm, "mid": v(90.53, -37.64) * mm, "end": v(89.6, -36.43) * mm});
            skLineSegment(sketch, "E13.34.6", {"start": v(91.63, -38.7) * mm, "end": v(92.53, -39.44) * mm});
            skArc(sketch, "E13.34.7", {"start": v(92.53, -39.44) * mm, "mid": v(93.53, -40.49) * mm, "end": v(94.28, -41.73) * mm});
            skArc(sketch, "E13.35.0", {"start": v(99.06, -17.42) * mm, "mid": v(100.48, -17.1) * mm, "end": v(101.78, -16.46) * mm});
            skLineSegment(sketch, "E13.35.1", {"start": v(97.9, -17.55) * mm, "end": v(99.06, -17.42) * mm});
            skArc(sketch, "E13.35.2", {"start": v(97.9, -17.55) * mm, "mid": v(96.4, -17.84) * mm, "end": v(94.97, -18.35) * mm});
            skArc(sketch, "E13.35.3", {"start": v(94.97, -18.35) * mm, "mid": v(93.47, -19.47) * mm, "end": v(92.64, -21.15) * mm});
            skArc(sketch, "E13.35.4", {"start": v(93.52, -24.67) * mm, "mid": v(92.66, -23.01) * mm, "end": v(92.64, -21.15) * mm});
            skArc(sketch, "E13.35.5", {"start": v(95.82, -26.67) * mm, "mid": v(94.6, -25.75) * mm, "end": v(93.52, -24.67) * mm});
            skLineSegment(sketch, "E13.35.6", {"start": v(95.82, -26.67) * mm, "end": v(96.8, -27.29) * mm});
            skArc(sketch, "E13.35.7", {"start": v(96.8, -27.29) * mm, "mid": v(97.94, -28.2) * mm, "end": v(98.84, -29.34) * mm});
            skArc(sketch, "E13.36.0", {"start": v(100.48, -4.6) * mm, "mid": v(101.84, -4.1) * mm, "end": v(103.05, -3.3) * mm});
            skLineSegment(sketch, "E13.36.1", {"start": v(99.34, -4.89) * mm, "end": v(100.48, -4.6) * mm});
            skArc(sketch, "E13.36.2", {"start": v(99.34, -4.89) * mm, "mid": v(97.9, -5.37) * mm, "end": v(96.53, -6.06) * mm});
            skArc(sketch, "E13.36.3", {"start": v(96.53, -6.06) * mm, "mid": v(95.2, -7.36) * mm, "end": v(94.59, -9.12) * mm});
            skArc(sketch, "E13.36.4", {"start": v(95.91, -12.5) * mm, "mid": v(94.85, -10.97) * mm, "end": v(94.59, -9.12) * mm});
            skArc(sketch, "E13.36.5", {"start": v(98.45, -14.2) * mm, "mid": v(97.12, -13.44) * mm, "end": v(95.91, -12.5) * mm});
            skLineSegment(sketch, "E13.36.6", {"start": v(98.45, -14.2) * mm, "end": v(99.5, -14.68) * mm});
            skArc(sketch, "E13.36.7", {"start": v(99.5, -14.68) * mm, "mid": v(100.74, -15.44) * mm, "end": v(101.78, -16.46) * mm});
            skArc(sketch, "E13.37.0", {"start": v(100.24, 8.28) * mm, "mid": v(101.53, 8.95) * mm, "end": v(102.63, 9.9) * mm});
            skLineSegment(sketch, "E13.37.1", {"start": v(99.15, 7.86) * mm, "end": v(100.24, 8.28) * mm});
            skArc(sketch, "E13.37.2", {"start": v(99.15, 7.86) * mm, "mid": v(97.78, 7.2) * mm, "end": v(96.52, 6.34) * mm});
            skArc(sketch, "E13.37.3", {"start": v(96.52, 6.34) * mm, "mid": v(95.35, 4.87) * mm, "end": v(94.98, 3.05) * mm});
            skArc(sketch, "E13.37.4", {"start": v(96.72, -0.14) * mm, "mid": v(95.47, 1.24) * mm, "end": v(94.98, 3.05) * mm});
            skArc(sketch, "E13.37.5", {"start": v(99.45, -1.49) * mm, "mid": v(98.04, -0.91) * mm, "end": v(96.72, -0.14) * mm});
            skLineSegment(sketch, "E13.37.6", {"start": v(99.45, -1.49) * mm, "end": v(100.56, -1.84) * mm});
            skArc(sketch, "E13.37.7", {"start": v(100.56, -1.84) * mm, "mid": v(101.9, -2.43) * mm, "end": v(103.05, -3.3) * mm});
            skArc(sketch, "E13.38.0", {"start": v(98.36, 21.03) * mm, "mid": v(99.55, 21.86) * mm, "end": v(100.52, 22.94) * mm});
            skLineSegment(sketch, "E13.38.1", {"start": v(97.33, 20.47) * mm, "end": v(98.36, 21.03) * mm});
            skArc(sketch, "E13.38.2", {"start": v(97.33, 20.47) * mm, "mid": v(96.06, 19.64) * mm, "end": v(94.91, 18.63) * mm});
            skArc(sketch, "E13.38.3", {"start": v(94.91, 18.63) * mm, "mid": v(93.95, 17.03) * mm, "end": v(93.8, 15.17) * mm});
            skArc(sketch, "E13.38.4", {"start": v(95.95, 12.23) * mm, "mid": v(94.53, 13.44) * mm, "end": v(93.8, 15.17) * mm});
            skArc(sketch, "E13.38.5", {"start": v(98.83, 11.24) * mm, "mid": v(97.35, 11.63) * mm, "end": v(95.95, 12.23) * mm});
            skLineSegment(sketch, "E13.38.6", {"start": v(98.83, 11.24) * mm, "end": v(99.97, 11.04) * mm});
            skArc(sketch, "E13.38.7", {"start": v(99.97, 11.04) * mm, "mid": v(101.37, 10.62) * mm, "end": v(102.63, 9.9) * mm});
            skArc(sketch, "E13.39.0", {"start": v(94.86, 33.43) * mm, "mid": v(95.93, 34.41) * mm, "end": v(96.76, 35.6) * mm});
            skLineSegment(sketch, "E13.39.1", {"start": v(93.92, 32.75) * mm, "end": v(94.86, 33.43) * mm});
            skArc(sketch, "E13.39.2", {"start": v(93.92, 32.75) * mm, "mid": v(92.76, 31.76) * mm, "end": v(91.75, 30.61) * mm});
            skArc(sketch, "E13.39.3", {"start": v(91.75, 30.61) * mm, "mid": v(91, 28.9) * mm, "end": v(91.1, 27.04) * mm});
            skArc(sketch, "E13.39.4", {"start": v(93.6, 24.4) * mm, "mid": v(92.03, 25.42) * mm, "end": v(91.1, 27.04) * mm});
            skArc(sketch, "E13.39.5", {"start": v(96.58, 23.79) * mm, "mid": v(95.06, 23.98) * mm, "end": v(93.6, 24.4) * mm});
            skLineSegment(sketch, "E13.39.6", {"start": v(96.58, 23.79) * mm, "end": v(97.74, 23.73) * mm});
            skArc(sketch, "E13.39.7", {"start": v(97.74, 23.73) * mm, "mid": v(99.17, 23.5) * mm, "end": v(100.52, 22.94) * mm});
            skArc(sketch, "E13.40.0", {"start": v(89.8, 45.3) * mm, "mid": v(90.75, 46.4) * mm, "end": v(91.41, 47.69) * mm});
            skLineSegment(sketch, "E13.40.1", {"start": v(88.96, 44.5) * mm, "end": v(89.8, 45.3) * mm});
            skArc(sketch, "E13.40.2", {"start": v(88.96, 44.5) * mm, "mid": v(87.93, 43.36) * mm, "end": v(87.08, 42.1) * mm});
            skArc(sketch, "E13.40.3", {"start": v(87.08, 42.1) * mm, "mid": v(86.56, 40.3) * mm, "end": v(86.9, 38.47) * mm});
            skArc(sketch, "E13.40.4", {"start": v(89.7, 36.17) * mm, "mid": v(88.03, 36.98) * mm, "end": v(86.9, 38.47) * mm});
            skArc(sketch, "E13.40.5", {"start": v(92.74, 35.94) * mm, "mid": v(91.22, 35.94) * mm, "end": v(89.7, 36.17) * mm});
            skLineSegment(sketch, "E13.40.6", {"start": v(92.74, 35.94) * mm, "end": v(93.9, 36.03) * mm});
            skArc(sketch, "E13.40.7", {"start": v(93.9, 36.03) * mm, "mid": v(95.36, 35.98) * mm, "end": v(96.76, 35.6) * mm});
            skArc(sketch, "E13.41.0", {"start": v(83.28, 56.4) * mm, "mid": v(84.07, 57.62) * mm, "end": v(84.56, 58.99) * mm});
            skLineSegment(sketch, "E13.41.1", {"start": v(82.54, 55.5) * mm, "end": v(83.28, 56.4) * mm});
            skArc(sketch, "E13.41.2", {"start": v(82.54, 55.5) * mm, "mid": v(81.67, 54.25) * mm, "end": v(80.99, 52.88) * mm});
            skArc(sketch, "E13.41.3", {"start": v(80.99, 52.88) * mm, "mid": v(80.7, 51.04) * mm, "end": v(81.26, 49.26) * mm});
            skArc(sketch, "E13.41.4", {"start": v(84.35, 47.34) * mm, "mid": v(82.57, 47.93) * mm, "end": v(81.26, 49.26) * mm});
            skArc(sketch, "E13.41.5", {"start": v(87.38, 47.5) * mm, "mid": v(85.87, 47.31) * mm, "end": v(84.35, 47.34) * mm});
            skLineSegment(sketch, "E13.41.6", {"start": v(87.38, 47.5) * mm, "end": v(88.53, 47.75) * mm});
            skArc(sketch, "E13.41.7", {"start": v(88.53, 47.75) * mm, "mid": v(89.97, 47.88) * mm, "end": v(91.41, 47.69) * mm});
            skArc(sketch, "E13.42.0", {"start": v(75.38, 66.59) * mm, "mid": v(76, 67.9) * mm, "end": v(76.32, 69.32) * mm});
            skLineSegment(sketch, "E13.42.1", {"start": v(74.76, 65.6) * mm, "end": v(75.38, 66.59) * mm});
            skArc(sketch, "E13.42.2", {"start": v(74.76, 65.6) * mm, "mid": v(74.06, 64.25) * mm, "end": v(73.56, 62.8) * mm});
            skArc(sketch, "E13.42.3", {"start": v(73.56, 62.8) * mm, "mid": v(73.5, 60.94) * mm, "end": v(74.3, 59.25) * mm});
            skArc(sketch, "E13.42.4", {"start": v(77.6, 57.74) * mm, "mid": v(75.77, 58.1) * mm, "end": v(74.3, 59.25) * mm});
            skArc(sketch, "E13.42.5", {"start": v(80.6, 58.3) * mm, "mid": v(79.12, 57.9) * mm, "end": v(77.6, 57.74) * mm});
            skLineSegment(sketch, "E13.42.6", {"start": v(80.6, 58.3) * mm, "end": v(81.7, 58.68) * mm});
            skArc(sketch, "E13.42.7", {"start": v(81.7, 58.68) * mm, "mid": v(83.11, 59) * mm, "end": v(84.56, 58.99) * mm});
            skArc(sketch, "E13.43.0", {"start": v(66.25, 75.68) * mm, "mid": v(66.7, 77.06) * mm, "end": v(66.83, 78.5) * mm});
            skLineSegment(sketch, "E13.43.1", {"start": v(65.76, 74.62) * mm, "end": v(66.25, 75.68) * mm});
            skArc(sketch, "E13.43.2", {"start": v(65.76, 74.62) * mm, "mid": v(65.23, 73.2) * mm, "end": v(64.92, 71.7) * mm});
            skArc(sketch, "E13.43.3", {"start": v(64.92, 71.7) * mm, "mid": v(65.1, 69.84) * mm, "end": v(66.1, 68.26) * mm});
            skArc(sketch, "E13.43.4", {"start": v(69.58, 67.19) * mm, "mid": v(67.71, 67.31) * mm, "end": v(66.1, 68.26) * mm});
            skArc(sketch, "E13.43.5", {"start": v(72.48, 68.12) * mm, "mid": v(71.06, 67.55) * mm, "end": v(69.58, 67.19) * mm});
            skLineSegment(sketch, "E13.43.6", {"start": v(72.48, 68.12) * mm, "end": v(73.52, 68.64) * mm});
            skArc(sketch, "E13.43.7", {"start": v(73.52, 68.64) * mm, "mid": v(74.88, 69.14) * mm, "end": v(76.32, 69.32) * mm});
            skArc(sketch, "E13.44.0", {"start": v(56.03, 83.53) * mm, "mid": v(56.3, 84.96) * mm, "end": v(56.25, 86.4) * mm});
            skLineSegment(sketch, "E13.44.1", {"start": v(55.68, 82.42) * mm, "end": v(56.03, 83.53) * mm});
            skArc(sketch, "E13.44.2", {"start": v(55.68, 82.42) * mm, "mid": v(55.34, 80.93) * mm, "end": v(55.22, 79.4) * mm});
            skArc(sketch, "E13.44.3", {"start": v(55.22, 79.4) * mm, "mid": v(55.64, 77.59) * mm, "end": v(56.84, 76.16) * mm});
            skArc(sketch, "E13.44.4", {"start": v(60.41, 75.53) * mm, "mid": v(58.55, 75.42) * mm, "end": v(56.84, 76.16) * mm});
            skArc(sketch, "E13.44.5", {"start": v(63.17, 76.83) * mm, "mid": v(61.84, 76.08) * mm, "end": v(60.41, 75.53) * mm});
            skLineSegment(sketch, "E13.44.6", {"start": v(63.17, 76.83) * mm, "end": v(64.14, 77.48) * mm});
            skArc(sketch, "E13.44.7", {"start": v(64.14, 77.48) * mm, "mid": v(65.43, 78.15) * mm, "end": v(66.83, 78.5) * mm});
            skArc(sketch, "E13.45.0", {"start": v(44.88, 90.01) * mm, "mid": v(44.97, 91.46) * mm, "end": v(44.73, 92.9) * mm});
            skLineSegment(sketch, "E13.45.1", {"start": v(44.68, 88.86) * mm, "end": v(44.88, 90.01) * mm});
            skArc(sketch, "E13.45.2", {"start": v(44.68, 88.86) * mm, "mid": v(44.54, 87.34) * mm, "end": v(44.62, 85.82) * mm});
            skArc(sketch, "E13.45.3", {"start": v(44.62, 85.82) * mm, "mid": v(45.26, 84.07) * mm, "end": v(46.63, 82.8) * mm});
            skArc(sketch, "E13.45.4", {"start": v(50.26, 82.64) * mm, "mid": v(48.43, 82.29) * mm, "end": v(46.63, 82.8) * mm});
            skArc(sketch, "E13.45.5", {"start": v(52.83, 84.28) * mm, "mid": v(51.6, 83.36) * mm, "end": v(50.26, 82.64) * mm});
            skLineSegment(sketch, "E13.45.6", {"start": v(52.83, 84.28) * mm, "end": v(53.7, 85.04) * mm});
            skArc(sketch, "E13.45.7", {"start": v(53.7, 85.04) * mm, "mid": v(54.9, 85.87) * mm, "end": v(56.25, 86.4) * mm});
            skArc(sketch, "E13.46.0", {"start": v(33, 95.01) * mm, "mid": v(32.9, 96.46) * mm, "end": v(32.49, 97.85) * mm});
            skLineSegment(sketch, "E13.46.1", {"start": v(32.95, 93.85) * mm, "end": v(33, 95.01) * mm});
            skArc(sketch, "E13.46.2", {"start": v(32.95, 93.85) * mm, "mid": v(33, 92.32) * mm, "end": v(33.27, 90.82) * mm});
            skArc(sketch, "E13.46.3", {"start": v(33.27, 90.82) * mm, "mid": v(34.14, 89.17) * mm, "end": v(35.66, 88.08) * mm});
            skArc(sketch, "E13.46.4", {"start": v(39.28, 88.39) * mm, "mid": v(37.5, 87.8) * mm, "end": v(35.66, 88.08) * mm});
            skArc(sketch, "E13.46.5", {"start": v(41.62, 90.34) * mm, "mid": v(40.52, 89.28) * mm, "end": v(39.28, 88.39) * mm});
            skLineSegment(sketch, "E13.46.6", {"start": v(41.62, 90.34) * mm, "end": v(42.39, 91.21) * mm});
            skArc(sketch, "E13.46.7", {"start": v(42.39, 91.21) * mm, "mid": v(43.47, 92.19) * mm, "end": v(44.73, 92.9) * mm});
            skArc(sketch, "E13.47.0", {"start": v(20.59, 98.45) * mm, "mid": v(20.3, 99.88) * mm, "end": v(19.7, 101.2) * mm});
            skLineSegment(sketch, "E13.47.1", {"start": v(20.68, 97.3) * mm, "end": v(20.59, 98.45) * mm});
            skArc(sketch, "E13.47.2", {"start": v(20.68, 97.3) * mm, "mid": v(20.92, 95.78) * mm, "end": v(21.39, 94.33) * mm});
            skArc(sketch, "E13.47.3", {"start": v(21.39, 94.33) * mm, "mid": v(22.46, 92.8) * mm, "end": v(24.1, 91.92) * mm});
            skArc(sketch, "E13.47.4", {"start": v(27.65, 92.69) * mm, "mid": v(25.97, 91.88) * mm, "end": v(24.1, 91.92) * mm});
            skArc(sketch, "E13.47.5", {"start": v(29.72, 94.92) * mm, "mid": v(28.77, 93.73) * mm, "end": v(27.65, 92.69) * mm});
            skLineSegment(sketch, "E13.47.6", {"start": v(29.72, 94.92) * mm, "end": v(30.38, 95.89) * mm});
            skArc(sketch, "E13.47.7", {"start": v(30.38, 95.89) * mm, "mid": v(31.32, 96.99) * mm, "end": v(32.49, 97.85) * mm});
            skArc(sketch, "E13.48.0", {"start": v(7.83, 100.28) * mm, "mid": v(7.37, 101.65) * mm, "end": v(6.6, 102.9) * mm});
            skLineSegment(sketch, "E13.48.1", {"start": v(8.07, 99.14) * mm, "end": v(7.83, 100.28) * mm});
            skArc(sketch, "E13.48.2", {"start": v(8.07, 99.14) * mm, "mid": v(8.5, 97.67) * mm, "end": v(9.15, 96.29) * mm});
            skArc(sketch, "E13.48.3", {"start": v(9.15, 96.29) * mm, "mid": v(10.4, 94.9) * mm, "end": v(12.15, 94.25) * mm});
            skArc(sketch, "E13.48.4", {"start": v(15.57, 95.46) * mm, "mid": v(14, 94.45) * mm, "end": v(12.15, 94.25) * mm});
            skArc(sketch, "E13.48.5", {"start": v(17.34, 97.94) * mm, "mid": v(16.55, 96.64) * mm, "end": v(15.57, 95.46) * mm});
            skLineSegment(sketch, "E13.48.6", {"start": v(17.34, 97.94) * mm, "end": v(17.87, 98.98) * mm});
            skArc(sketch, "E13.48.7", {"start": v(17.87, 98.98) * mm, "mid": v(18.66, 100.2) * mm, "end": v(19.7, 101.2) * mm});
            skCircle(sketch, "E14", {"center": v(0, 0) * mm, "radius": 101.49 * mm});
            skSolve(sketch);
        }
        {
            var Q0;
            Q0=makeQuery(id+"F0.imprint","IMPRINT",FACE,{"disambiguationData":[TD([[makeQuery(id+"F0.imprint","IMPRINT",EDGE,{"derivedFrom":sQuery(id+"F0.wireOp",EDGE,"E3")}),-1.0]])]});
            extrude(context, id + "F1", {"entities" : qUnion([Q0]), "endBound" : BoundingType.SYMMETRIC, "depth" : 3.5 * mm});
        }
        {
            var Q0;
            Q0=makeQuery(id+"F0.imprint","IMPRINT",FACE,{"disambiguationData":[TD([[makeQuery(id+"F0.imprint","IMPRINT",EDGE,{"derivedFrom":sQuery(id+"F0.wireOp",EDGE,"E1")}),-1.0]])]});
            extrude(context, id + "F2", {"entities" : qUnion([Q0]), "operationType" : NewBodyOperationType.ADD, "endBound" : BoundingType.SYMMETRIC, "depth" : 4.5 * mm});
        }
        {
            var Q0;
            {var subQ0=sQuery(id+"F0.wireOp",EDGE,"E5");var subQ1=sQuery(id+"F0.wireOp",EDGE,"E0");Q0=makeQuery(id+"F2.opExtrude","SWEPT_EDGE",EDGE,{"disambiguationData":[OSD([subQ1,subQ0]),TDD([makeQuery(id+"F0.imprint","INTERSECT",VERTEX,{"disambiguationData":[OD(0.0)],"derivedFrom":[subQ1,subQ0]})])]});}
            var Q1;
            {var subQ0=sQuery(id+"F0.wireOp",EDGE,"E5");var subQ1=sQuery(id+"F0.wireOp",EDGE,"E0");Q1=makeQuery(id+"F2.opExtrude","SWEPT_EDGE",EDGE,{"disambiguationData":[OSD([subQ1,subQ0]),TDD([makeQuery(id+"F0.imprint","INTERSECT",VERTEX,{"disambiguationData":[OD(1.0)],"derivedFrom":[subQ1,subQ0]})])]});}
            fillet(context, id + "F3", {"entities" : qUnion([Q0, Q1]), "radius" : 5.08 * mm, "tangentPropagation" : true, "allowEdgeOverflow" : false});
        }
        {
            var Q0;
            Q0=makeQuery(id+"F2.opExtrude","CAP_FACE",FACE,{"disambiguationData":[OSD([sQuery(id+"F0.wireOp",EDGE,"E0"),sQuery(id+"F0.wireOp",EDGE,"E1"),sQuery(id+"F0.wireOp",EDGE,"E2.1.0"),sQuery(id+"F0.wireOp",EDGE,"E2.2.0"),sQuery(id+"F0.wireOp",EDGE,"E2.3.0"),sQuery(id+"F0.wireOp",EDGE,"E2.4.0"),sQuery(id+"F0.wireOp",EDGE,"E4"),sQuery(id+"F0.wireOp",EDGE,"E5")])],"isStart":false});
            var sketch = newSketch(context, id + "F4", { "sketchPlane" : qUnion([Q0])});
            skLineSegment(sketch, "E15", {"start": v(48.72, -50.37) * mm, "end": v(60.8, -62.85) * mm});
            skLineSegment(sketch, "E16", {"start": v(69.03, 12.11) * mm, "end": v(86.13, 15.11) * mm});
            skArc(sketch, "E17", {"start": v(60.8, -62.85) * mm, "mid": v(65.07, -58.42) * mm, "end": v(69.02, -53.7) * mm});
            skArc(sketch, "E18", {"start": v(48.72, -50.37) * mm, "mid": v(52.15, -46.82) * mm, "end": v(55.31, -43.03) * mm});
            skLineSegment(sketch, "E19", {"start": v(70.04, 2.3) * mm, "end": v(87.4, 2.88) * mm});
            skLineSegment(sketch, "E20", {"start": v(70.08, 0.47) * mm, "end": v(87.44, 0.59) * mm});
            skLineSegment(sketch, "E21", {"start": v(69.45, -9.37) * mm, "end": v(86.66, -11.7) * mm});
            skLineSegment(sketch, "E22", {"start": v(69.18, -11.18) * mm, "end": v(86.33, -13.95) * mm});
            skLineSegment(sketch, "E23", {"start": v(66.93, -20.78) * mm, "end": v(83.51, -25.93) * mm});
            skLineSegment(sketch, "E24", {"start": v(66.36, -22.53) * mm, "end": v(82.8, -28.1) * mm});
            skLineSegment(sketch, "E25", {"start": v(62.54, -31.62) * mm, "end": v(78.04, -39.45) * mm});
            skLineSegment(sketch, "E26", {"start": v(61.7, -33.24) * mm, "end": v(76.98, -41.48) * mm});
            skLineSegment(sketch, "E27", {"start": v(56.42, -41.57) * mm, "end": v(70.4, -51.87) * mm});
            skLineSegment(sketch, "E28", {"start": v(55.31, -43.03) * mm, "end": v(69.02, -53.7) * mm});
            skArc(sketch, "E29.trimOffspring", {"start": v(70.04, 2.3) * mm, "mid": v(69.7, 7.23) * mm, "end": v(69.03, 12.11) * mm});
            skArc(sketch, "E30.trimOffspring", {"start": v(69.45, -9.37) * mm, "mid": v(69.94, -4.46) * mm, "end": v(70.08, 0.47) * mm});
            skArc(sketch, "E31.trimOffspring", {"start": v(66.93, -20.78) * mm, "mid": v(68.22, -16.02) * mm, "end": v(69.18, -11.18) * mm});
            skArc(sketch, "E32.trimOffspring", {"start": v(62.54, -31.62) * mm, "mid": v(64.61, -27.14) * mm, "end": v(66.36, -22.53) * mm});
            skArc(sketch, "E33.trimOffspring", {"start": v(56.42, -41.57) * mm, "mid": v(59.2, -37.5) * mm, "end": v(61.7, -33.24) * mm});
            skArc(sketch, "E34.trimOffspring", {"start": v(70.4, -51.87) * mm, "mid": v(73.87, -46.8) * mm, "end": v(76.98, -41.48) * mm});
            skArc(sketch, "E35.trimOffspring", {"start": v(78.04, -39.45) * mm, "mid": v(80.62, -33.86) * mm, "end": v(82.8, -28.1) * mm});
            skArc(sketch, "E36.trimOffspring", {"start": v(83.51, -25.93) * mm, "mid": v(85.13, -20) * mm, "end": v(86.33, -13.95) * mm});
            skArc(sketch, "E37.trimOffspring", {"start": v(87.4, 2.88) * mm, "mid": v(86.98, 9.02) * mm, "end": v(86.13, 15.11) * mm});
            skArc(sketch, "E38.trimOffspring", {"start": v(86.66, -11.7) * mm, "mid": v(87.27, -5.57) * mm, "end": v(87.44, 0.59) * mm});
            skArc(sketch, "E39.1.0", {"start": v(30.37, 63.16) * mm, "mid": v(25.85, 65.14) * mm, "end": v(21.2, 66.8) * mm});
            skArc(sketch, "E39.1.1", {"start": v(19.45, 67.33) * mm, "mid": v(14.67, 68.53) * mm, "end": v(9.81, 69.39) * mm});
            skArc(sketch, "E39.1.2", {"start": v(24.27, 84.01) * mm, "mid": v(18.3, 85.51) * mm, "end": v(12.24, 86.59) * mm});
            skLineSegment(sketch, "E39.1.3", {"start": v(9.81, 69.39) * mm, "end": v(12.24, 86.59) * mm});
            skArc(sketch, "E39.1.4", {"start": v(40.45, 57.23) * mm, "mid": v(36.32, 59.93) * mm, "end": v(32.01, 62.34) * mm});
            skArc(sketch, "E39.1.5", {"start": v(78.56, 38.4) * mm, "mid": v(75.67, 43.83) * mm, "end": v(72.4, 49.05) * mm});
            skLineSegment(sketch, "E39.1.6", {"start": v(19.45, 67.33) * mm, "end": v(24.27, 84.01) * mm});
            skArc(sketch, "E39.1.7", {"start": v(62.96, 30.77) * mm, "mid": v(60.64, 35.13) * mm, "end": v(58.02, 39.3) * mm});
            skArc(sketch, "E39.1.8", {"start": v(56.97, 40.81) * mm, "mid": v(53.96, 44.72) * mm, "end": v(50.68, 48.4) * mm});
            skArc(sketch, "E39.1.9", {"start": v(37.9, 78.8) * mm, "mid": v(32.26, 81.28) * mm, "end": v(26.46, 83.35) * mm});
            skLineSegment(sketch, "E39.1.10", {"start": v(30.37, 63.16) * mm, "end": v(37.9, 78.8) * mm});
            skLineSegment(sketch, "E39.1.11", {"start": v(21.2, 66.8) * mm, "end": v(26.46, 83.35) * mm});
            skLineSegment(sketch, "E39.1.12", {"start": v(62.96, 30.77) * mm, "end": v(78.56, 38.4) * mm});
            skLineSegment(sketch, "E39.1.13", {"start": v(40.45, 57.23) * mm, "end": v(50.47, 71.41) * mm});
            skLineSegment(sketch, "E39.1.14", {"start": v(58.02, 39.3) * mm, "end": v(72.4, 49.05) * mm});
            skLineSegment(sketch, "E39.1.15", {"start": v(41.93, 56.15) * mm, "end": v(52.32, 70.07) * mm});
            skArc(sketch, "E39.1.16", {"start": v(50.47, 71.41) * mm, "mid": v(45.32, 74.79) * mm, "end": v(39.95, 77.79) * mm});
            skArc(sketch, "E39.1.17", {"start": v(71.09, 50.92) * mm, "mid": v(67.33, 55.8) * mm, "end": v(63.24, 60.4) * mm});
            skLineSegment(sketch, "E39.1.18", {"start": v(49.4, 49.71) * mm, "end": v(61.64, 62.03) * mm});
            skLineSegment(sketch, "E39.1.19", {"start": v(56.97, 40.81) * mm, "end": v(71.09, 50.92) * mm});
            skLineSegment(sketch, "E39.1.20", {"start": v(32.01, 62.34) * mm, "end": v(39.95, 77.79) * mm});
            skArc(sketch, "E39.1.21", {"start": v(61.64, 62.03) * mm, "mid": v(57.12, 66.21) * mm, "end": v(52.32, 70.07) * mm});
            skLineSegment(sketch, "E39.1.22", {"start": v(50.68, 48.4) * mm, "end": v(63.24, 60.4) * mm});
            skArc(sketch, "E39.1.23", {"start": v(49.4, 49.71) * mm, "mid": v(45.78, 53.06) * mm, "end": v(41.93, 56.15) * mm});
            skArc(sketch, "E39.2.0", {"start": v(-50.68, 48.4) * mm, "mid": v(-53.96, 44.72) * mm, "end": v(-56.97, 40.81) * mm});
            skArc(sketch, "E39.2.1", {"start": v(-58.02, 39.3) * mm, "mid": v(-60.64, 35.13) * mm, "end": v(-62.96, 30.77) * mm});
            skArc(sketch, "E39.2.2", {"start": v(-72.4, 49.05) * mm, "mid": v(-75.67, 43.83) * mm, "end": v(-78.56, 38.4) * mm});
            skLineSegment(sketch, "E39.2.3", {"start": v(-62.96, 30.77) * mm, "end": v(-78.56, 38.4) * mm});
            skArc(sketch, "E39.2.4", {"start": v(-41.93, 56.15) * mm, "mid": v(-45.78, 53.06) * mm, "end": v(-49.4, 49.71) * mm});
            skArc(sketch, "E39.2.5", {"start": v(-12.24, 86.59) * mm, "mid": v(-18.3, 85.51) * mm, "end": v(-24.27, 84.01) * mm});
            skLineSegment(sketch, "E39.2.6", {"start": v(-58.02, 39.3) * mm, "end": v(-72.4, 49.05) * mm});
            skArc(sketch, "E39.2.7", {"start": v(-9.81, 69.39) * mm, "mid": v(-14.67, 68.53) * mm, "end": v(-19.45, 67.33) * mm});
            skArc(sketch, "E39.2.8", {"start": v(-21.2, 66.8) * mm, "mid": v(-25.85, 65.14) * mm, "end": v(-30.37, 63.16) * mm});
            skArc(sketch, "E39.2.9", {"start": v(-63.24, 60.4) * mm, "mid": v(-67.33, 55.8) * mm, "end": v(-71.09, 50.92) * mm});
            skLineSegment(sketch, "E39.2.10", {"start": v(-50.68, 48.4) * mm, "end": v(-63.24, 60.4) * mm});
            skLineSegment(sketch, "E39.2.11", {"start": v(-56.97, 40.81) * mm, "end": v(-71.09, 50.92) * mm});
            skLineSegment(sketch, "E39.2.12", {"start": v(-9.81, 69.39) * mm, "end": v(-12.24, 86.59) * mm});
            skLineSegment(sketch, "E39.2.13", {"start": v(-41.93, 56.15) * mm, "end": v(-52.32, 70.07) * mm});
            skLineSegment(sketch, "E39.2.14", {"start": v(-19.45, 67.33) * mm, "end": v(-24.27, 84.01) * mm});
            skLineSegment(sketch, "E39.2.15", {"start": v(-40.45, 57.23) * mm, "end": v(-50.47, 71.41) * mm});
            skArc(sketch, "E39.2.16", {"start": v(-52.32, 70.07) * mm, "mid": v(-57.12, 66.21) * mm, "end": v(-61.64, 62.03) * mm});
            skArc(sketch, "E39.2.17", {"start": v(-26.46, 83.35) * mm, "mid": v(-32.26, 81.28) * mm, "end": v(-37.9, 78.8) * mm});
            skLineSegment(sketch, "E39.2.18", {"start": v(-32.01, 62.34) * mm, "end": v(-39.95, 77.79) * mm});
            skLineSegment(sketch, "E39.2.19", {"start": v(-21.2, 66.8) * mm, "end": v(-26.46, 83.35) * mm});
            skLineSegment(sketch, "E39.2.20", {"start": v(-49.4, 49.71) * mm, "end": v(-61.64, 62.03) * mm});
            skArc(sketch, "E39.2.21", {"start": v(-39.95, 77.79) * mm, "mid": v(-45.32, 74.79) * mm, "end": v(-50.47, 71.41) * mm});
            skLineSegment(sketch, "E39.2.22", {"start": v(-30.37, 63.16) * mm, "end": v(-37.9, 78.8) * mm});
            skArc(sketch, "E39.2.23", {"start": v(-32.01, 62.34) * mm, "mid": v(-36.32, 59.93) * mm, "end": v(-40.45, 57.23) * mm});
            skArc(sketch, "E39.3.0", {"start": v(-61.7, -33.24) * mm, "mid": v(-59.2, -37.5) * mm, "end": v(-56.42, -41.57) * mm});
            skArc(sketch, "E39.3.1", {"start": v(-55.31, -43.03) * mm, "mid": v(-52.15, -46.82) * mm, "end": v(-48.72, -50.37) * mm});
            skArc(sketch, "E39.3.2", {"start": v(-69.02, -53.7) * mm, "mid": v(-65.07, -58.42) * mm, "end": v(-60.8, -62.85) * mm});
            skLineSegment(sketch, "E39.3.3", {"start": v(-48.72, -50.37) * mm, "end": v(-60.8, -62.85) * mm});
            skArc(sketch, "E39.3.4", {"start": v(-66.36, -22.53) * mm, "mid": v(-64.61, -27.14) * mm, "end": v(-62.54, -31.62) * mm});
            skArc(sketch, "E39.3.5", {"start": v(-86.13, 15.11) * mm, "mid": v(-86.98, 9.02) * mm, "end": v(-87.4, 2.88) * mm});
            skLineSegment(sketch, "E39.3.6", {"start": v(-55.31, -43.03) * mm, "end": v(-69.02, -53.7) * mm});
            skArc(sketch, "E39.3.7", {"start": v(-69.03, 12.11) * mm, "mid": v(-69.7, 7.23) * mm, "end": v(-70.04, 2.3) * mm});
            skArc(sketch, "E39.3.8", {"start": v(-70.08, 0.47) * mm, "mid": v(-69.94, -4.46) * mm, "end": v(-69.45, -9.37) * mm});
            skArc(sketch, "E39.3.9", {"start": v(-76.98, -41.48) * mm, "mid": v(-73.87, -46.8) * mm, "end": v(-70.4, -51.87) * mm});
            skLineSegment(sketch, "E39.3.10", {"start": v(-61.7, -33.24) * mm, "end": v(-76.98, -41.48) * mm});
            skLineSegment(sketch, "E39.3.11", {"start": v(-56.42, -41.57) * mm, "end": v(-70.4, -51.87) * mm});
            skLineSegment(sketch, "E39.3.12", {"start": v(-69.03, 12.11) * mm, "end": v(-86.13, 15.11) * mm});
            skLineSegment(sketch, "E39.3.13", {"start": v(-66.36, -22.53) * mm, "end": v(-82.8, -28.1) * mm});
            skLineSegment(sketch, "E39.3.14", {"start": v(-70.04, 2.3) * mm, "end": v(-87.4, 2.88) * mm});
            skLineSegment(sketch, "E39.3.15", {"start": v(-66.93, -20.78) * mm, "end": v(-83.51, -25.93) * mm});
            skArc(sketch, "E39.3.16", {"start": v(-82.8, -28.1) * mm, "mid": v(-80.62, -33.86) * mm, "end": v(-78.04, -39.45) * mm});
            skArc(sketch, "E39.3.17", {"start": v(-87.44, 0.59) * mm, "mid": v(-87.27, -5.57) * mm, "end": v(-86.66, -11.7) * mm});
            skLineSegment(sketch, "E39.3.18", {"start": v(-69.18, -11.18) * mm, "end": v(-86.33, -13.95) * mm});
            skLineSegment(sketch, "E39.3.19", {"start": v(-70.08, 0.47) * mm, "end": v(-87.44, 0.59) * mm});
            skLineSegment(sketch, "E39.3.20", {"start": v(-62.54, -31.62) * mm, "end": v(-78.04, -39.45) * mm});
            skArc(sketch, "E39.3.21", {"start": v(-86.33, -13.95) * mm, "mid": v(-85.13, -20) * mm, "end": v(-83.51, -25.93) * mm});
            skLineSegment(sketch, "E39.3.22", {"start": v(-69.45, -9.37) * mm, "end": v(-86.66, -11.7) * mm});
            skArc(sketch, "E39.3.23", {"start": v(-69.18, -11.18) * mm, "mid": v(-68.22, -16.02) * mm, "end": v(-66.93, -20.78) * mm});
            skSolve(sketch);
        }
        {
            var Q0;
            Q0=makeQuery(id+"F4.imprint","IMPRINT",FACE,{"disambiguationData":[TD([[makeQuery(id+"F4.imprint","IMPRINT",EDGE,{"derivedFrom":sQuery(id+"F4.wireOp",EDGE,"E39.3.1")}),-1.0]])]});
            var Q1;
            Q1=makeQuery(id+"F4.imprint","IMPRINT",FACE,{"disambiguationData":[TD([[makeQuery(id+"F4.imprint","IMPRINT",EDGE,{"derivedFrom":sQuery(id+"F4.wireOp",EDGE,"E39.3.0")}),-1.0]])]});
            var Q2;
            Q2=makeQuery(id+"F4.imprint","IMPRINT",FACE,{"disambiguationData":[TD([[makeQuery(id+"F4.imprint","IMPRINT",EDGE,{"derivedFrom":sQuery(id+"F4.wireOp",EDGE,"E39.3.5")}),1.0]])]});
            var Q3;
            Q3=makeQuery(id+"F4.imprint","IMPRINT",FACE,{"disambiguationData":[TD([[makeQuery(id+"F4.imprint","IMPRINT",EDGE,{"derivedFrom":sQuery(id+"F4.wireOp",EDGE,"E39.2.1")}),-1.0]])]});
            var Q4;
            Q4=makeQuery(id+"F4.imprint","IMPRINT",FACE,{"disambiguationData":[TD([[makeQuery(id+"F4.imprint","IMPRINT",EDGE,{"derivedFrom":sQuery(id+"F4.wireOp",EDGE,"E39.2.0")}),-1.0]])]});
            var Q5;
            Q5=makeQuery(id+"F4.imprint","IMPRINT",FACE,{"disambiguationData":[TD([[makeQuery(id+"F4.imprint","IMPRINT",EDGE,{"derivedFrom":sQuery(id+"F4.wireOp",EDGE,"E39.2.5")}),1.0]])]});
            var Q6;
            Q6=makeQuery(id+"F4.imprint","IMPRINT",FACE,{"disambiguationData":[TD([[makeQuery(id+"F4.imprint","IMPRINT",EDGE,{"derivedFrom":sQuery(id+"F4.wireOp",EDGE,"E39.1.1")}),-1.0]])]});
            var Q7;
            Q7=makeQuery(id+"F4.imprint","IMPRINT",FACE,{"disambiguationData":[TD([[makeQuery(id+"F4.imprint","IMPRINT",EDGE,{"derivedFrom":sQuery(id+"F4.wireOp",EDGE,"E39.1.0")}),-1.0]])]});
            var Q8;
            Q8=makeQuery(id+"F4.imprint","IMPRINT",FACE,{"disambiguationData":[TD([[makeQuery(id+"F4.imprint","IMPRINT",EDGE,{"derivedFrom":sQuery(id+"F4.wireOp",EDGE,"E39.1.5")}),1.0]])]});
            var Q9;
            Q9=makeQuery(id+"F4.imprint","IMPRINT",FACE,{"disambiguationData":[TD([[makeQuery(id+"F4.imprint","IMPRINT",EDGE,{"derivedFrom":sQuery(id+"F4.wireOp",EDGE,"E16")}),-1.0]])]});
            var Q10;
            Q10=makeQuery(id+"F4.imprint","IMPRINT",FACE,{"disambiguationData":[TD([[makeQuery(id+"F4.imprint","IMPRINT",EDGE,{"derivedFrom":sQuery(id+"F4.wireOp",EDGE,"E20")}),-1.0]])]});
            var Q11;
            Q11=makeQuery(id+"F4.imprint","IMPRINT",FACE,{"disambiguationData":[TD([[makeQuery(id+"F4.imprint","IMPRINT",EDGE,{"derivedFrom":sQuery(id+"F4.wireOp",EDGE,"E15")}),1.0]])]});
            extrude(context, id + "F5", {"entities" : qUnion([Q0, Q1, Q2, Q3, Q4, Q5, Q6, Q7, Q8, Q9, Q10, Q11]), "operationType" : NewBodyOperationType.REMOVE, "oppositeDirection" : true, "depth" : 4.5 * mm});
        }
        {
            var Q0;
            Q0=makeQuery(id+"F4.imprint","IMPRINT",FACE,{"disambiguationData":[TD([[makeQuery(id+"F4.imprint","IMPRINT",EDGE,{"derivedFrom":sQuery(id+"F4.wireOp",EDGE,"E39.3.4")}),-1.0]])]});
            var Q1;
            Q1=makeQuery(id+"F4.imprint","IMPRINT",FACE,{"disambiguationData":[TD([[makeQuery(id+"F4.imprint","IMPRINT",EDGE,{"derivedFrom":sQuery(id+"F4.wireOp",EDGE,"E39.3.15")}),-1.0]])]});
            var Q2;
            Q2=makeQuery(id+"F4.imprint","IMPRINT",FACE,{"disambiguationData":[TD([[makeQuery(id+"F4.imprint","IMPRINT",EDGE,{"derivedFrom":sQuery(id+"F4.wireOp",EDGE,"E39.3.8")}),-1.0]])]});
            var Q3;
            Q3=makeQuery(id+"F4.imprint","IMPRINT",FACE,{"disambiguationData":[TD([[makeQuery(id+"F4.imprint","IMPRINT",EDGE,{"derivedFrom":sQuery(id+"F4.wireOp",EDGE,"E39.2.4")}),-1.0]])]});
            var Q4;
            Q4=makeQuery(id+"F4.imprint","IMPRINT",FACE,{"disambiguationData":[TD([[makeQuery(id+"F4.imprint","IMPRINT",EDGE,{"derivedFrom":sQuery(id+"F4.wireOp",EDGE,"E39.2.15")}),-1.0]])]});
            var Q5;
            Q5=makeQuery(id+"F4.imprint","IMPRINT",FACE,{"disambiguationData":[TD([[makeQuery(id+"F4.imprint","IMPRINT",EDGE,{"derivedFrom":sQuery(id+"F4.wireOp",EDGE,"E39.2.8")}),-1.0]])]});
            var Q6;
            Q6=makeQuery(id+"F4.imprint","IMPRINT",FACE,{"disambiguationData":[TD([[makeQuery(id+"F4.imprint","IMPRINT",EDGE,{"derivedFrom":sQuery(id+"F4.wireOp",EDGE,"E39.1.4")}),-1.0]])]});
            var Q7;
            Q7=makeQuery(id+"F4.imprint","IMPRINT",FACE,{"disambiguationData":[TD([[makeQuery(id+"F4.imprint","IMPRINT",EDGE,{"derivedFrom":sQuery(id+"F4.wireOp",EDGE,"E39.1.15")}),-1.0]])]});
            var Q8;
            Q8=makeQuery(id+"F4.imprint","IMPRINT",FACE,{"disambiguationData":[TD([[makeQuery(id+"F4.imprint","IMPRINT",EDGE,{"derivedFrom":sQuery(id+"F4.wireOp",EDGE,"E39.1.8")}),-1.0]])]});
            var Q9;
            Q9=makeQuery(id+"F4.imprint","IMPRINT",FACE,{"disambiguationData":[TD([[makeQuery(id+"F4.imprint","IMPRINT",EDGE,{"derivedFrom":sQuery(id+"F4.wireOp",EDGE,"E22")}),-1.0]])]});
            var Q10;
            Q10=makeQuery(id+"F4.imprint","IMPRINT",FACE,{"disambiguationData":[TD([[makeQuery(id+"F4.imprint","IMPRINT",EDGE,{"derivedFrom":sQuery(id+"F4.wireOp",EDGE,"E24")}),-1.0]])]});
            var Q11;
            Q11=makeQuery(id+"F4.imprint","IMPRINT",FACE,{"disambiguationData":[TD([[makeQuery(id+"F4.imprint","IMPRINT",EDGE,{"derivedFrom":sQuery(id+"F4.wireOp",EDGE,"E26")}),-1.0]])]});
            extrude(context, id + "F6", {"entities" : qUnion([Q0, Q1, Q2, Q3, Q4, Q5, Q6, Q7, Q8, Q9, Q10, Q11]), "operationType" : NewBodyOperationType.REMOVE, "oppositeDirection" : true, "depth" : 2.5 * mm});
        }
        {
            var Q0;
            Q0=makeQuery(id+"F5.boolean.opBoolean","COPY",EDGE,{"derivedFrom":makeQuery(id+"F5.opExtrude","SWEPT_EDGE",EDGE,{"disambiguationData":[OSD([sQuery(id+"F4.wireOp",EDGE,"E39.3.1"),sQuery(id+"F4.wireOp",EDGE,"E39.3.6")])]})});
            var Q1;
            Q1=makeQuery(id+"F5.boolean.opBoolean","COPY",EDGE,{"derivedFrom":makeQuery(id+"F5.opExtrude","SWEPT_EDGE",EDGE,{"disambiguationData":[OSD([sQuery(id+"F4.wireOp",EDGE,"E39.3.0"),sQuery(id+"F4.wireOp",EDGE,"E39.3.10")])]})});
            var Q2;
            Q2=makeQuery(id+"F6.boolean.opBoolean","COPY",EDGE,{"derivedFrom":makeQuery(id+"F6.opExtrude","SWEPT_EDGE",EDGE,{"disambiguationData":[OSD([sQuery(id+"F4.wireOp",EDGE,"E39.3.4"),sQuery(id+"F4.wireOp",EDGE,"E39.3.13")])]})});
            var Q3;
            Q3=makeQuery(id+"F6.boolean.opBoolean","COPY",EDGE,{"derivedFrom":makeQuery(id+"F6.opExtrude","SWEPT_EDGE",EDGE,{"disambiguationData":[OSD([sQuery(id+"F4.wireOp",EDGE,"E39.3.18"),sQuery(id+"F4.wireOp",EDGE,"E39.3.23")])]})});
            var Q4;
            Q4=makeQuery(id+"F6.boolean.opBoolean","COPY",EDGE,{"derivedFrom":makeQuery(id+"F6.opExtrude","SWEPT_EDGE",EDGE,{"disambiguationData":[OSD([sQuery(id+"F4.wireOp",EDGE,"E39.3.8"),sQuery(id+"F4.wireOp",EDGE,"E39.3.19")])]})});
            var Q5;
            Q5=makeQuery(id+"F5.boolean.opBoolean","COPY",EDGE,{"derivedFrom":makeQuery(id+"F5.opExtrude","SWEPT_EDGE",EDGE,{"disambiguationData":[OSD([sQuery(id+"F4.wireOp",EDGE,"E39.3.7"),sQuery(id+"F4.wireOp",EDGE,"E39.3.12")])]})});
            var Q6;
            Q6=makeQuery(id+"F6.boolean.opBoolean","COPY",EDGE,{"derivedFrom":makeQuery(id+"F6.opExtrude","SWEPT_EDGE",EDGE,{"disambiguationData":[OSD([sQuery(id+"F4.wireOp",EDGE,"E39.3.8"),sQuery(id+"F4.wireOp",EDGE,"E39.3.22")])]})});
            var Q7;
            Q7=makeQuery(id+"F6.boolean.opBoolean","COPY",EDGE,{"derivedFrom":makeQuery(id+"F6.opExtrude","SWEPT_EDGE",EDGE,{"disambiguationData":[OSD([sQuery(id+"F4.wireOp",EDGE,"E39.3.15"),sQuery(id+"F4.wireOp",EDGE,"E39.3.23")])]})});
            var Q8;
            Q8=makeQuery(id+"F5.boolean.opBoolean","COPY",EDGE,{"derivedFrom":makeQuery(id+"F5.opExtrude","SWEPT_EDGE",EDGE,{"disambiguationData":[OSD([sQuery(id+"F4.wireOp",EDGE,"E39.3.7"),sQuery(id+"F4.wireOp",EDGE,"E39.3.14")])]})});
            var Q9;
            Q9=makeQuery(id+"F6.boolean.opBoolean","COPY",EDGE,{"derivedFrom":makeQuery(id+"F6.opExtrude","SWEPT_EDGE",EDGE,{"disambiguationData":[OSD([sQuery(id+"F4.wireOp",EDGE,"E39.3.4"),sQuery(id+"F4.wireOp",EDGE,"E39.3.20")])]})});
            var Q10;
            Q10=makeQuery(id+"F5.boolean.opBoolean","COPY",EDGE,{"derivedFrom":makeQuery(id+"F5.opExtrude","SWEPT_EDGE",EDGE,{"disambiguationData":[OSD([sQuery(id+"F4.wireOp",EDGE,"E39.3.0"),sQuery(id+"F4.wireOp",EDGE,"E39.3.11")])]})});
            var Q11;
            Q11=makeQuery(id+"F5.boolean.opBoolean","COPY",EDGE,{"derivedFrom":makeQuery(id+"F5.opExtrude","SWEPT_EDGE",EDGE,{"disambiguationData":[OSD([sQuery(id+"F4.wireOp",EDGE,"E39.3.1"),sQuery(id+"F4.wireOp",EDGE,"E39.3.3")])]})});
            var Q12;
            Q12=makeQuery(id+"F5.boolean.opBoolean","COPY",EDGE,{"derivedFrom":makeQuery(id+"F5.opExtrude","SWEPT_EDGE",EDGE,{"disambiguationData":[OSD([sQuery(id+"F4.wireOp",EDGE,"E39.3.5"),sQuery(id+"F4.wireOp",EDGE,"E39.3.14")])]})});
            var Q13;
            Q13=makeQuery(id+"F6.boolean.opBoolean","COPY",EDGE,{"derivedFrom":makeQuery(id+"F6.opExtrude","SWEPT_EDGE",EDGE,{"disambiguationData":[OSD([sQuery(id+"F4.wireOp",EDGE,"E39.3.17"),sQuery(id+"F4.wireOp",EDGE,"E39.3.22")])]})});
            var Q14;
            Q14=makeQuery(id+"F6.boolean.opBoolean","COPY",EDGE,{"derivedFrom":makeQuery(id+"F6.opExtrude","SWEPT_EDGE",EDGE,{"disambiguationData":[OSD([sQuery(id+"F4.wireOp",EDGE,"E39.3.15"),sQuery(id+"F4.wireOp",EDGE,"E39.3.21")])]})});
            var Q15;
            Q15=makeQuery(id+"F6.boolean.opBoolean","COPY",EDGE,{"derivedFrom":makeQuery(id+"F6.opExtrude","SWEPT_EDGE",EDGE,{"disambiguationData":[OSD([sQuery(id+"F4.wireOp",EDGE,"E39.3.16"),sQuery(id+"F4.wireOp",EDGE,"E39.3.20")])]})});
            var Q16;
            Q16=makeQuery(id+"F5.boolean.opBoolean","COPY",EDGE,{"derivedFrom":makeQuery(id+"F5.opExtrude","SWEPT_EDGE",EDGE,{"disambiguationData":[OSD([sQuery(id+"F4.wireOp",EDGE,"E39.3.9"),sQuery(id+"F4.wireOp",EDGE,"E39.3.11")])]})});
            var Q17;
            Q17=makeQuery(id+"F5.boolean.opBoolean","COPY",EDGE,{"derivedFrom":makeQuery(id+"F5.opExtrude","SWEPT_EDGE",EDGE,{"disambiguationData":[OSD([sQuery(id+"F4.wireOp",EDGE,"E39.3.2"),sQuery(id+"F4.wireOp",EDGE,"E39.3.3")])]})});
            var Q18;
            Q18=makeQuery(id+"F5.boolean.opBoolean","COPY",EDGE,{"derivedFrom":makeQuery(id+"F5.opExtrude","SWEPT_EDGE",EDGE,{"disambiguationData":[OSD([sQuery(id+"F4.wireOp",EDGE,"E39.3.2"),sQuery(id+"F4.wireOp",EDGE,"E39.3.6")])]})});
            var Q19;
            Q19=makeQuery(id+"F5.boolean.opBoolean","COPY",EDGE,{"derivedFrom":makeQuery(id+"F5.opExtrude","SWEPT_EDGE",EDGE,{"disambiguationData":[OSD([sQuery(id+"F4.wireOp",EDGE,"E39.3.9"),sQuery(id+"F4.wireOp",EDGE,"E39.3.10")])]})});
            var Q20;
            Q20=makeQuery(id+"F6.boolean.opBoolean","COPY",EDGE,{"derivedFrom":makeQuery(id+"F6.opExtrude","SWEPT_EDGE",EDGE,{"disambiguationData":[OSD([sQuery(id+"F4.wireOp",EDGE,"E39.3.13"),sQuery(id+"F4.wireOp",EDGE,"E39.3.16")])]})});
            var Q21;
            Q21=makeQuery(id+"F6.boolean.opBoolean","COPY",EDGE,{"derivedFrom":makeQuery(id+"F6.opExtrude","SWEPT_EDGE",EDGE,{"disambiguationData":[OSD([sQuery(id+"F4.wireOp",EDGE,"E39.3.18"),sQuery(id+"F4.wireOp",EDGE,"E39.3.21")])]})});
            var Q22;
            Q22=makeQuery(id+"F6.boolean.opBoolean","COPY",EDGE,{"derivedFrom":makeQuery(id+"F6.opExtrude","SWEPT_EDGE",EDGE,{"disambiguationData":[OSD([sQuery(id+"F4.wireOp",EDGE,"E39.3.17"),sQuery(id+"F4.wireOp",EDGE,"E39.3.19")])]})});
            var Q23;
            Q23=makeQuery(id+"F5.boolean.opBoolean","COPY",EDGE,{"derivedFrom":makeQuery(id+"F5.opExtrude","SWEPT_EDGE",EDGE,{"disambiguationData":[OSD([sQuery(id+"F4.wireOp",EDGE,"E39.3.5"),sQuery(id+"F4.wireOp",EDGE,"E39.3.12")])]})});
            var Q24;
            Q24=makeQuery(id+"F5.boolean.opBoolean","COPY",EDGE,{"derivedFrom":makeQuery(id+"F5.opExtrude","SWEPT_EDGE",EDGE,{"disambiguationData":[OSD([sQuery(id+"F4.wireOp",EDGE,"E39.2.1"),sQuery(id+"F4.wireOp",EDGE,"E39.2.6")])]})});
            var Q25;
            Q25=makeQuery(id+"F5.boolean.opBoolean","COPY",EDGE,{"derivedFrom":makeQuery(id+"F5.opExtrude","SWEPT_EDGE",EDGE,{"disambiguationData":[OSD([sQuery(id+"F4.wireOp",EDGE,"E39.2.0"),sQuery(id+"F4.wireOp",EDGE,"E39.2.10")])]})});
            var Q26;
            Q26=makeQuery(id+"F6.boolean.opBoolean","COPY",EDGE,{"derivedFrom":makeQuery(id+"F6.opExtrude","SWEPT_EDGE",EDGE,{"disambiguationData":[OSD([sQuery(id+"F4.wireOp",EDGE,"E39.2.4"),sQuery(id+"F4.wireOp",EDGE,"E39.2.13")])]})});
            var Q27;
            Q27=makeQuery(id+"F6.boolean.opBoolean","COPY",EDGE,{"derivedFrom":makeQuery(id+"F6.opExtrude","SWEPT_EDGE",EDGE,{"disambiguationData":[OSD([sQuery(id+"F4.wireOp",EDGE,"E39.2.18"),sQuery(id+"F4.wireOp",EDGE,"E39.2.23")])]})});
            var Q28;
            Q28=makeQuery(id+"F6.boolean.opBoolean","COPY",EDGE,{"derivedFrom":makeQuery(id+"F6.opExtrude","SWEPT_EDGE",EDGE,{"disambiguationData":[OSD([sQuery(id+"F4.wireOp",EDGE,"E39.2.8"),sQuery(id+"F4.wireOp",EDGE,"E39.2.19")])]})});
            var Q29;
            Q29=makeQuery(id+"F5.boolean.opBoolean","COPY",EDGE,{"derivedFrom":makeQuery(id+"F5.opExtrude","SWEPT_EDGE",EDGE,{"disambiguationData":[OSD([sQuery(id+"F4.wireOp",EDGE,"E39.2.7"),sQuery(id+"F4.wireOp",EDGE,"E39.2.12")])]})});
            var Q30;
            Q30=makeQuery(id+"F5.boolean.opBoolean","COPY",EDGE,{"derivedFrom":makeQuery(id+"F5.opExtrude","SWEPT_EDGE",EDGE,{"disambiguationData":[OSD([sQuery(id+"F4.wireOp",EDGE,"E39.2.7"),sQuery(id+"F4.wireOp",EDGE,"E39.2.14")])]})});
            var Q31;
            Q31=makeQuery(id+"F6.boolean.opBoolean","COPY",EDGE,{"derivedFrom":makeQuery(id+"F6.opExtrude","SWEPT_EDGE",EDGE,{"disambiguationData":[OSD([sQuery(id+"F4.wireOp",EDGE,"E39.2.8"),sQuery(id+"F4.wireOp",EDGE,"E39.2.22")])]})});
            var Q32;
            Q32=makeQuery(id+"F6.boolean.opBoolean","COPY",EDGE,{"derivedFrom":makeQuery(id+"F6.opExtrude","SWEPT_EDGE",EDGE,{"disambiguationData":[OSD([sQuery(id+"F4.wireOp",EDGE,"E39.2.15"),sQuery(id+"F4.wireOp",EDGE,"E39.2.23")])]})});
            var Q33;
            Q33=makeQuery(id+"F6.boolean.opBoolean","COPY",EDGE,{"derivedFrom":makeQuery(id+"F6.opExtrude","SWEPT_EDGE",EDGE,{"disambiguationData":[OSD([sQuery(id+"F4.wireOp",EDGE,"E39.2.4"),sQuery(id+"F4.wireOp",EDGE,"E39.2.20")])]})});
            var Q34;
            Q34=makeQuery(id+"F5.boolean.opBoolean","COPY",EDGE,{"derivedFrom":makeQuery(id+"F5.opExtrude","SWEPT_EDGE",EDGE,{"disambiguationData":[OSD([sQuery(id+"F4.wireOp",EDGE,"E39.2.0"),sQuery(id+"F4.wireOp",EDGE,"E39.2.11")])]})});
            var Q35;
            Q35=makeQuery(id+"F5.boolean.opBoolean","COPY",EDGE,{"derivedFrom":makeQuery(id+"F5.opExtrude","SWEPT_EDGE",EDGE,{"disambiguationData":[OSD([sQuery(id+"F4.wireOp",EDGE,"E39.2.1"),sQuery(id+"F4.wireOp",EDGE,"E39.2.3")])]})});
            var Q36;
            Q36=makeQuery(id+"F5.boolean.opBoolean","COPY",EDGE,{"derivedFrom":makeQuery(id+"F5.opExtrude","SWEPT_EDGE",EDGE,{"disambiguationData":[OSD([sQuery(id+"F4.wireOp",EDGE,"E39.2.2"),sQuery(id+"F4.wireOp",EDGE,"E39.2.6")])]})});
            var Q37;
            Q37=makeQuery(id+"F5.boolean.opBoolean","COPY",EDGE,{"derivedFrom":makeQuery(id+"F5.opExtrude","SWEPT_EDGE",EDGE,{"disambiguationData":[OSD([sQuery(id+"F4.wireOp",EDGE,"E39.2.9"),sQuery(id+"F4.wireOp",EDGE,"E39.2.10")])]})});
            var Q38;
            Q38=makeQuery(id+"F6.boolean.opBoolean","COPY",EDGE,{"derivedFrom":makeQuery(id+"F6.opExtrude","SWEPT_EDGE",EDGE,{"disambiguationData":[OSD([sQuery(id+"F4.wireOp",EDGE,"E39.2.13"),sQuery(id+"F4.wireOp",EDGE,"E39.2.16")])]})});
            var Q39;
            Q39=makeQuery(id+"F6.boolean.opBoolean","COPY",EDGE,{"derivedFrom":makeQuery(id+"F6.opExtrude","SWEPT_EDGE",EDGE,{"disambiguationData":[OSD([sQuery(id+"F4.wireOp",EDGE,"E39.2.18"),sQuery(id+"F4.wireOp",EDGE,"E39.2.21")])]})});
            var Q40;
            Q40=makeQuery(id+"F6.boolean.opBoolean","COPY",EDGE,{"derivedFrom":makeQuery(id+"F6.opExtrude","SWEPT_EDGE",EDGE,{"disambiguationData":[OSD([sQuery(id+"F4.wireOp",EDGE,"E39.2.17"),sQuery(id+"F4.wireOp",EDGE,"E39.2.19")])]})});
            var Q41;
            Q41=makeQuery(id+"F5.boolean.opBoolean","COPY",EDGE,{"derivedFrom":makeQuery(id+"F5.opExtrude","SWEPT_EDGE",EDGE,{"disambiguationData":[OSD([sQuery(id+"F4.wireOp",EDGE,"E39.2.5"),sQuery(id+"F4.wireOp",EDGE,"E39.2.12")])]})});
            var Q42;
            Q42=makeQuery(id+"F5.boolean.opBoolean","COPY",EDGE,{"derivedFrom":makeQuery(id+"F5.opExtrude","SWEPT_EDGE",EDGE,{"disambiguationData":[OSD([sQuery(id+"F4.wireOp",EDGE,"E39.2.5"),sQuery(id+"F4.wireOp",EDGE,"E39.2.14")])]})});
            var Q43;
            Q43=makeQuery(id+"F6.boolean.opBoolean","COPY",EDGE,{"derivedFrom":makeQuery(id+"F6.opExtrude","SWEPT_EDGE",EDGE,{"disambiguationData":[OSD([sQuery(id+"F4.wireOp",EDGE,"E39.2.17"),sQuery(id+"F4.wireOp",EDGE,"E39.2.22")])]})});
            var Q44;
            Q44=makeQuery(id+"F6.boolean.opBoolean","COPY",EDGE,{"derivedFrom":makeQuery(id+"F6.opExtrude","SWEPT_EDGE",EDGE,{"disambiguationData":[OSD([sQuery(id+"F4.wireOp",EDGE,"E39.2.15"),sQuery(id+"F4.wireOp",EDGE,"E39.2.21")])]})});
            var Q45;
            Q45=makeQuery(id+"F6.boolean.opBoolean","COPY",EDGE,{"derivedFrom":makeQuery(id+"F6.opExtrude","SWEPT_EDGE",EDGE,{"disambiguationData":[OSD([sQuery(id+"F4.wireOp",EDGE,"E39.2.16"),sQuery(id+"F4.wireOp",EDGE,"E39.2.20")])]})});
            var Q46;
            Q46=makeQuery(id+"F5.boolean.opBoolean","COPY",EDGE,{"derivedFrom":makeQuery(id+"F5.opExtrude","SWEPT_EDGE",EDGE,{"disambiguationData":[OSD([sQuery(id+"F4.wireOp",EDGE,"E39.2.9"),sQuery(id+"F4.wireOp",EDGE,"E39.2.11")])]})});
            var Q47;
            Q47=makeQuery(id+"F5.boolean.opBoolean","COPY",EDGE,{"derivedFrom":makeQuery(id+"F5.opExtrude","SWEPT_EDGE",EDGE,{"disambiguationData":[OSD([sQuery(id+"F4.wireOp",EDGE,"E39.2.2"),sQuery(id+"F4.wireOp",EDGE,"E39.2.3")])]})});
            var Q48;
            Q48=makeQuery(id+"F5.boolean.opBoolean","COPY",EDGE,{"derivedFrom":makeQuery(id+"F5.opExtrude","SWEPT_EDGE",EDGE,{"disambiguationData":[OSD([sQuery(id+"F4.wireOp",EDGE,"E39.1.5"),sQuery(id+"F4.wireOp",EDGE,"E39.1.14")])]})});
            var Q49;
            Q49=makeQuery(id+"F6.boolean.opBoolean","COPY",EDGE,{"derivedFrom":makeQuery(id+"F6.opExtrude","SWEPT_EDGE",EDGE,{"disambiguationData":[OSD([sQuery(id+"F4.wireOp",EDGE,"E39.1.17"),sQuery(id+"F4.wireOp",EDGE,"E39.1.22")])]})});
            var Q50;
            Q50=makeQuery(id+"F6.boolean.opBoolean","COPY",EDGE,{"derivedFrom":makeQuery(id+"F6.opExtrude","SWEPT_EDGE",EDGE,{"disambiguationData":[OSD([sQuery(id+"F4.wireOp",EDGE,"E39.1.15"),sQuery(id+"F4.wireOp",EDGE,"E39.1.21")])]})});
            var Q51;
            Q51=makeQuery(id+"F6.boolean.opBoolean","COPY",EDGE,{"derivedFrom":makeQuery(id+"F6.opExtrude","SWEPT_EDGE",EDGE,{"disambiguationData":[OSD([sQuery(id+"F4.wireOp",EDGE,"E39.1.16"),sQuery(id+"F4.wireOp",EDGE,"E39.1.20")])]})});
            var Q52;
            Q52=makeQuery(id+"F5.boolean.opBoolean","COPY",EDGE,{"derivedFrom":makeQuery(id+"F5.opExtrude","SWEPT_EDGE",EDGE,{"disambiguationData":[OSD([sQuery(id+"F4.wireOp",EDGE,"E39.1.9"),sQuery(id+"F4.wireOp",EDGE,"E39.1.11")])]})});
            var Q53;
            Q53=makeQuery(id+"F5.boolean.opBoolean","COPY",EDGE,{"derivedFrom":makeQuery(id+"F5.opExtrude","SWEPT_EDGE",EDGE,{"disambiguationData":[OSD([sQuery(id+"F4.wireOp",EDGE,"E39.1.2"),sQuery(id+"F4.wireOp",EDGE,"E39.1.3")])]})});
            var Q54;
            Q54=makeQuery(id+"F5.boolean.opBoolean","COPY",EDGE,{"derivedFrom":makeQuery(id+"F5.opExtrude","SWEPT_EDGE",EDGE,{"disambiguationData":[OSD([sQuery(id+"F4.wireOp",EDGE,"E39.1.2"),sQuery(id+"F4.wireOp",EDGE,"E39.1.6")])]})});
            var Q55;
            Q55=makeQuery(id+"F5.boolean.opBoolean","COPY",EDGE,{"derivedFrom":makeQuery(id+"F5.opExtrude","SWEPT_EDGE",EDGE,{"disambiguationData":[OSD([sQuery(id+"F4.wireOp",EDGE,"E39.1.9"),sQuery(id+"F4.wireOp",EDGE,"E39.1.10")])]})});
            var Q56;
            Q56=makeQuery(id+"F6.boolean.opBoolean","COPY",EDGE,{"derivedFrom":makeQuery(id+"F6.opExtrude","SWEPT_EDGE",EDGE,{"disambiguationData":[OSD([sQuery(id+"F4.wireOp",EDGE,"E39.1.13"),sQuery(id+"F4.wireOp",EDGE,"E39.1.16")])]})});
            var Q57;
            Q57=makeQuery(id+"F6.boolean.opBoolean","COPY",EDGE,{"derivedFrom":makeQuery(id+"F6.opExtrude","SWEPT_EDGE",EDGE,{"disambiguationData":[OSD([sQuery(id+"F4.wireOp",EDGE,"E39.1.18"),sQuery(id+"F4.wireOp",EDGE,"E39.1.21")])]})});
            var Q58;
            Q58=makeQuery(id+"F6.boolean.opBoolean","COPY",EDGE,{"derivedFrom":makeQuery(id+"F6.opExtrude","SWEPT_EDGE",EDGE,{"disambiguationData":[OSD([sQuery(id+"F4.wireOp",EDGE,"E39.1.17"),sQuery(id+"F4.wireOp",EDGE,"E39.1.19")])]})});
            var Q59;
            Q59=makeQuery(id+"F5.boolean.opBoolean","COPY",EDGE,{"derivedFrom":makeQuery(id+"F5.opExtrude","SWEPT_EDGE",EDGE,{"disambiguationData":[OSD([sQuery(id+"F4.wireOp",EDGE,"E39.1.5"),sQuery(id+"F4.wireOp",EDGE,"E39.1.12")])]})});
            var Q60;
            Q60=makeQuery(id+"F5.boolean.opBoolean","COPY",EDGE,{"derivedFrom":makeQuery(id+"F5.opExtrude","SWEPT_EDGE",EDGE,{"disambiguationData":[OSD([sQuery(id+"F4.wireOp",EDGE,"E39.1.7"),sQuery(id+"F4.wireOp",EDGE,"E39.1.14")])]})});
            var Q61;
            Q61=makeQuery(id+"F6.boolean.opBoolean","COPY",EDGE,{"derivedFrom":makeQuery(id+"F6.opExtrude","SWEPT_EDGE",EDGE,{"disambiguationData":[OSD([sQuery(id+"F4.wireOp",EDGE,"E39.1.8"),sQuery(id+"F4.wireOp",EDGE,"E39.1.22")])]})});
            var Q62;
            Q62=makeQuery(id+"F6.boolean.opBoolean","COPY",EDGE,{"derivedFrom":makeQuery(id+"F6.opExtrude","SWEPT_EDGE",EDGE,{"disambiguationData":[OSD([sQuery(id+"F4.wireOp",EDGE,"E39.1.15"),sQuery(id+"F4.wireOp",EDGE,"E39.1.23")])]})});
            var Q63;
            Q63=makeQuery(id+"F6.boolean.opBoolean","COPY",EDGE,{"derivedFrom":makeQuery(id+"F6.opExtrude","SWEPT_EDGE",EDGE,{"disambiguationData":[OSD([sQuery(id+"F4.wireOp",EDGE,"E39.1.4"),sQuery(id+"F4.wireOp",EDGE,"E39.1.20")])]})});
            var Q64;
            Q64=makeQuery(id+"F5.boolean.opBoolean","COPY",EDGE,{"derivedFrom":makeQuery(id+"F5.opExtrude","SWEPT_EDGE",EDGE,{"disambiguationData":[OSD([sQuery(id+"F4.wireOp",EDGE,"E39.1.0"),sQuery(id+"F4.wireOp",EDGE,"E39.1.11")])]})});
            var Q65;
            Q65=makeQuery(id+"F5.boolean.opBoolean","COPY",EDGE,{"derivedFrom":makeQuery(id+"F5.opExtrude","SWEPT_EDGE",EDGE,{"disambiguationData":[OSD([sQuery(id+"F4.wireOp",EDGE,"E39.1.1"),sQuery(id+"F4.wireOp",EDGE,"E39.1.3")])]})});
            var Q66;
            Q66=makeQuery(id+"F5.boolean.opBoolean","COPY",EDGE,{"derivedFrom":makeQuery(id+"F5.opExtrude","SWEPT_EDGE",EDGE,{"disambiguationData":[OSD([sQuery(id+"F4.wireOp",EDGE,"E39.1.1"),sQuery(id+"F4.wireOp",EDGE,"E39.1.6")])]})});
            var Q67;
            Q67=makeQuery(id+"F5.boolean.opBoolean","COPY",EDGE,{"derivedFrom":makeQuery(id+"F5.opExtrude","SWEPT_EDGE",EDGE,{"disambiguationData":[OSD([sQuery(id+"F4.wireOp",EDGE,"E39.1.0"),sQuery(id+"F4.wireOp",EDGE,"E39.1.10")])]})});
            var Q68;
            Q68=makeQuery(id+"F6.boolean.opBoolean","COPY",EDGE,{"derivedFrom":makeQuery(id+"F6.opExtrude","SWEPT_EDGE",EDGE,{"disambiguationData":[OSD([sQuery(id+"F4.wireOp",EDGE,"E39.1.4"),sQuery(id+"F4.wireOp",EDGE,"E39.1.13")])]})});
            var Q69;
            Q69=makeQuery(id+"F6.boolean.opBoolean","COPY",EDGE,{"derivedFrom":makeQuery(id+"F6.opExtrude","SWEPT_EDGE",EDGE,{"disambiguationData":[OSD([sQuery(id+"F4.wireOp",EDGE,"E39.1.18"),sQuery(id+"F4.wireOp",EDGE,"E39.1.23")])]})});
            var Q70;
            Q70=makeQuery(id+"F6.boolean.opBoolean","COPY",EDGE,{"derivedFrom":makeQuery(id+"F6.opExtrude","SWEPT_EDGE",EDGE,{"disambiguationData":[OSD([sQuery(id+"F4.wireOp",EDGE,"E39.1.8"),sQuery(id+"F4.wireOp",EDGE,"E39.1.19")])]})});
            var Q71;
            Q71=makeQuery(id+"F5.boolean.opBoolean","COPY",EDGE,{"derivedFrom":makeQuery(id+"F5.opExtrude","SWEPT_EDGE",EDGE,{"disambiguationData":[OSD([sQuery(id+"F4.wireOp",EDGE,"E39.1.7"),sQuery(id+"F4.wireOp",EDGE,"E39.1.12")])]})});
            var Q72;
            Q72=makeQuery(id+"F5.boolean.opBoolean","COPY",EDGE,{"derivedFrom":makeQuery(id+"F5.opExtrude","SWEPT_EDGE",EDGE,{"disambiguationData":[OSD([sQuery(id+"F4.wireOp",EDGE,"E16"),sQuery(id+"F4.wireOp",EDGE,"E29.trimOffspring")])]})});
            var Q73;
            Q73=makeQuery(id+"F5.boolean.opBoolean","COPY",EDGE,{"derivedFrom":makeQuery(id+"F5.opExtrude","SWEPT_EDGE",EDGE,{"disambiguationData":[OSD([sQuery(id+"F4.wireOp",EDGE,"E20"),sQuery(id+"F4.wireOp",EDGE,"E30.trimOffspring")])]})});
            var Q74;
            Q74=makeQuery(id+"F6.boolean.opBoolean","COPY",EDGE,{"derivedFrom":makeQuery(id+"F6.opExtrude","SWEPT_EDGE",EDGE,{"disambiguationData":[OSD([sQuery(id+"F4.wireOp",EDGE,"E22"),sQuery(id+"F4.wireOp",EDGE,"E31.trimOffspring")])]})});
            var Q75;
            Q75=makeQuery(id+"F6.boolean.opBoolean","COPY",EDGE,{"derivedFrom":makeQuery(id+"F6.opExtrude","SWEPT_EDGE",EDGE,{"disambiguationData":[OSD([sQuery(id+"F4.wireOp",EDGE,"E24"),sQuery(id+"F4.wireOp",EDGE,"E32.trimOffspring")])]})});
            var Q76;
            Q76=makeQuery(id+"F6.boolean.opBoolean","COPY",EDGE,{"derivedFrom":makeQuery(id+"F6.opExtrude","SWEPT_EDGE",EDGE,{"disambiguationData":[OSD([sQuery(id+"F4.wireOp",EDGE,"E26"),sQuery(id+"F4.wireOp",EDGE,"E33.trimOffspring")])]})});
            var Q77;
            Q77=makeQuery(id+"F5.boolean.opBoolean","COPY",EDGE,{"derivedFrom":makeQuery(id+"F5.opExtrude","SWEPT_EDGE",EDGE,{"disambiguationData":[OSD([sQuery(id+"F4.wireOp",EDGE,"E18"),sQuery(id+"F4.wireOp",EDGE,"E28")])]})});
            var Q78;
            Q78=makeQuery(id+"F5.boolean.opBoolean","COPY",EDGE,{"derivedFrom":makeQuery(id+"F5.opExtrude","SWEPT_EDGE",EDGE,{"disambiguationData":[OSD([sQuery(id+"F4.wireOp",EDGE,"E19"),sQuery(id+"F4.wireOp",EDGE,"E29.trimOffspring")])]})});
            var Q79;
            Q79=makeQuery(id+"F5.boolean.opBoolean","COPY",EDGE,{"derivedFrom":makeQuery(id+"F5.opExtrude","SWEPT_EDGE",EDGE,{"disambiguationData":[OSD([sQuery(id+"F4.wireOp",EDGE,"E21"),sQuery(id+"F4.wireOp",EDGE,"E30.trimOffspring")])]})});
            var Q80;
            Q80=makeQuery(id+"F6.boolean.opBoolean","COPY",EDGE,{"derivedFrom":makeQuery(id+"F6.opExtrude","SWEPT_EDGE",EDGE,{"disambiguationData":[OSD([sQuery(id+"F4.wireOp",EDGE,"E23"),sQuery(id+"F4.wireOp",EDGE,"E31.trimOffspring")])]})});
            var Q81;
            Q81=makeQuery(id+"F6.boolean.opBoolean","COPY",EDGE,{"derivedFrom":makeQuery(id+"F6.opExtrude","SWEPT_EDGE",EDGE,{"disambiguationData":[OSD([sQuery(id+"F4.wireOp",EDGE,"E25"),sQuery(id+"F4.wireOp",EDGE,"E32.trimOffspring")])]})});
            var Q82;
            Q82=makeQuery(id+"F6.boolean.opBoolean","COPY",EDGE,{"derivedFrom":makeQuery(id+"F6.opExtrude","SWEPT_EDGE",EDGE,{"disambiguationData":[OSD([sQuery(id+"F4.wireOp",EDGE,"E27"),sQuery(id+"F4.wireOp",EDGE,"E33.trimOffspring")])]})});
            var Q83;
            Q83=makeQuery(id+"F5.boolean.opBoolean","COPY",EDGE,{"derivedFrom":makeQuery(id+"F5.opExtrude","SWEPT_EDGE",EDGE,{"disambiguationData":[OSD([sQuery(id+"F4.wireOp",EDGE,"E15"),sQuery(id+"F4.wireOp",EDGE,"E18")])]})});
            var Q84;
            Q84=makeQuery(id+"F5.boolean.opBoolean","COPY",EDGE,{"derivedFrom":makeQuery(id+"F5.opExtrude","SWEPT_EDGE",EDGE,{"disambiguationData":[OSD([sQuery(id+"F4.wireOp",EDGE,"E17"),sQuery(id+"F4.wireOp",EDGE,"E28")])]})});
            var Q85;
            Q85=makeQuery(id+"F5.boolean.opBoolean","COPY",EDGE,{"derivedFrom":makeQuery(id+"F5.opExtrude","SWEPT_EDGE",EDGE,{"disambiguationData":[OSD([sQuery(id+"F4.wireOp",EDGE,"E19"),sQuery(id+"F4.wireOp",EDGE,"E37.trimOffspring")])]})});
            var Q86;
            Q86=makeQuery(id+"F5.boolean.opBoolean","COPY",EDGE,{"derivedFrom":makeQuery(id+"F5.opExtrude","SWEPT_EDGE",EDGE,{"disambiguationData":[OSD([sQuery(id+"F4.wireOp",EDGE,"E21"),sQuery(id+"F4.wireOp",EDGE,"E38.trimOffspring")])]})});
            var Q87;
            Q87=makeQuery(id+"F6.boolean.opBoolean","COPY",EDGE,{"derivedFrom":makeQuery(id+"F6.opExtrude","SWEPT_EDGE",EDGE,{"disambiguationData":[OSD([sQuery(id+"F4.wireOp",EDGE,"E23"),sQuery(id+"F4.wireOp",EDGE,"E36.trimOffspring")])]})});
            var Q88;
            Q88=makeQuery(id+"F6.boolean.opBoolean","COPY",EDGE,{"derivedFrom":makeQuery(id+"F6.opExtrude","SWEPT_EDGE",EDGE,{"disambiguationData":[OSD([sQuery(id+"F4.wireOp",EDGE,"E25"),sQuery(id+"F4.wireOp",EDGE,"E35.trimOffspring")])]})});
            var Q89;
            Q89=makeQuery(id+"F6.boolean.opBoolean","COPY",EDGE,{"derivedFrom":makeQuery(id+"F6.opExtrude","SWEPT_EDGE",EDGE,{"disambiguationData":[OSD([sQuery(id+"F4.wireOp",EDGE,"E27"),sQuery(id+"F4.wireOp",EDGE,"E34.trimOffspring")])]})});
            var Q90;
            Q90=makeQuery(id+"F5.boolean.opBoolean","COPY",EDGE,{"derivedFrom":makeQuery(id+"F5.opExtrude","SWEPT_EDGE",EDGE,{"disambiguationData":[OSD([sQuery(id+"F4.wireOp",EDGE,"E15"),sQuery(id+"F4.wireOp",EDGE,"E17")])]})});
            var Q91;
            Q91=makeQuery(id+"F6.boolean.opBoolean","COPY",EDGE,{"derivedFrom":makeQuery(id+"F6.opExtrude","SWEPT_EDGE",EDGE,{"disambiguationData":[OSD([sQuery(id+"F4.wireOp",EDGE,"E26"),sQuery(id+"F4.wireOp",EDGE,"E34.trimOffspring")])]})});
            var Q92;
            Q92=makeQuery(id+"F6.boolean.opBoolean","COPY",EDGE,{"derivedFrom":makeQuery(id+"F6.opExtrude","SWEPT_EDGE",EDGE,{"disambiguationData":[OSD([sQuery(id+"F4.wireOp",EDGE,"E24"),sQuery(id+"F4.wireOp",EDGE,"E35.trimOffspring")])]})});
            var Q93;
            Q93=makeQuery(id+"F6.boolean.opBoolean","COPY",EDGE,{"derivedFrom":makeQuery(id+"F6.opExtrude","SWEPT_EDGE",EDGE,{"disambiguationData":[OSD([sQuery(id+"F4.wireOp",EDGE,"E22"),sQuery(id+"F4.wireOp",EDGE,"E36.trimOffspring")])]})});
            var Q94;
            Q94=makeQuery(id+"F5.boolean.opBoolean","COPY",EDGE,{"derivedFrom":makeQuery(id+"F5.opExtrude","SWEPT_EDGE",EDGE,{"disambiguationData":[OSD([sQuery(id+"F4.wireOp",EDGE,"E20"),sQuery(id+"F4.wireOp",EDGE,"E38.trimOffspring")])]})});
            var Q95;
            Q95=makeQuery(id+"F5.boolean.opBoolean","COPY",EDGE,{"derivedFrom":makeQuery(id+"F5.opExtrude","SWEPT_EDGE",EDGE,{"disambiguationData":[OSD([sQuery(id+"F4.wireOp",EDGE,"E16"),sQuery(id+"F4.wireOp",EDGE,"E37.trimOffspring")])]})});
            fillet(context, id + "F7", {"entities" : qUnion([Q0, Q1, Q2, Q3, Q4, Q5, Q6, Q7, Q8, Q9, Q10, Q11, Q12, Q13, Q14, Q15, Q16, Q17, Q18, Q19, Q20, Q21, Q22, Q23, Q24, Q25, Q26, Q27, Q28, Q29, Q30, Q31, Q32, Q33, Q34, Q35, Q36, Q37, Q38, Q39, Q40, Q41, Q42, Q43, Q44, Q45, Q46, Q47, Q48, Q49, Q50, Q51, Q52, Q53, Q54, Q55, Q56, Q57, Q58, Q59, Q60, Q61, Q62, Q63, Q64, Q65, Q66, Q67, Q68, Q69, Q70, Q71, Q72, Q73, Q74, Q75, Q76, Q77, Q78, Q79, Q80, Q81, Q82, Q83, Q84, Q85, Q86, Q87, Q88, Q89, Q90, Q91, Q92, Q93, Q94, Q95]), "radius" : 2 * mm, "tangentPropagation" : true, "allowEdgeOverflow" : false});
        }
    });
